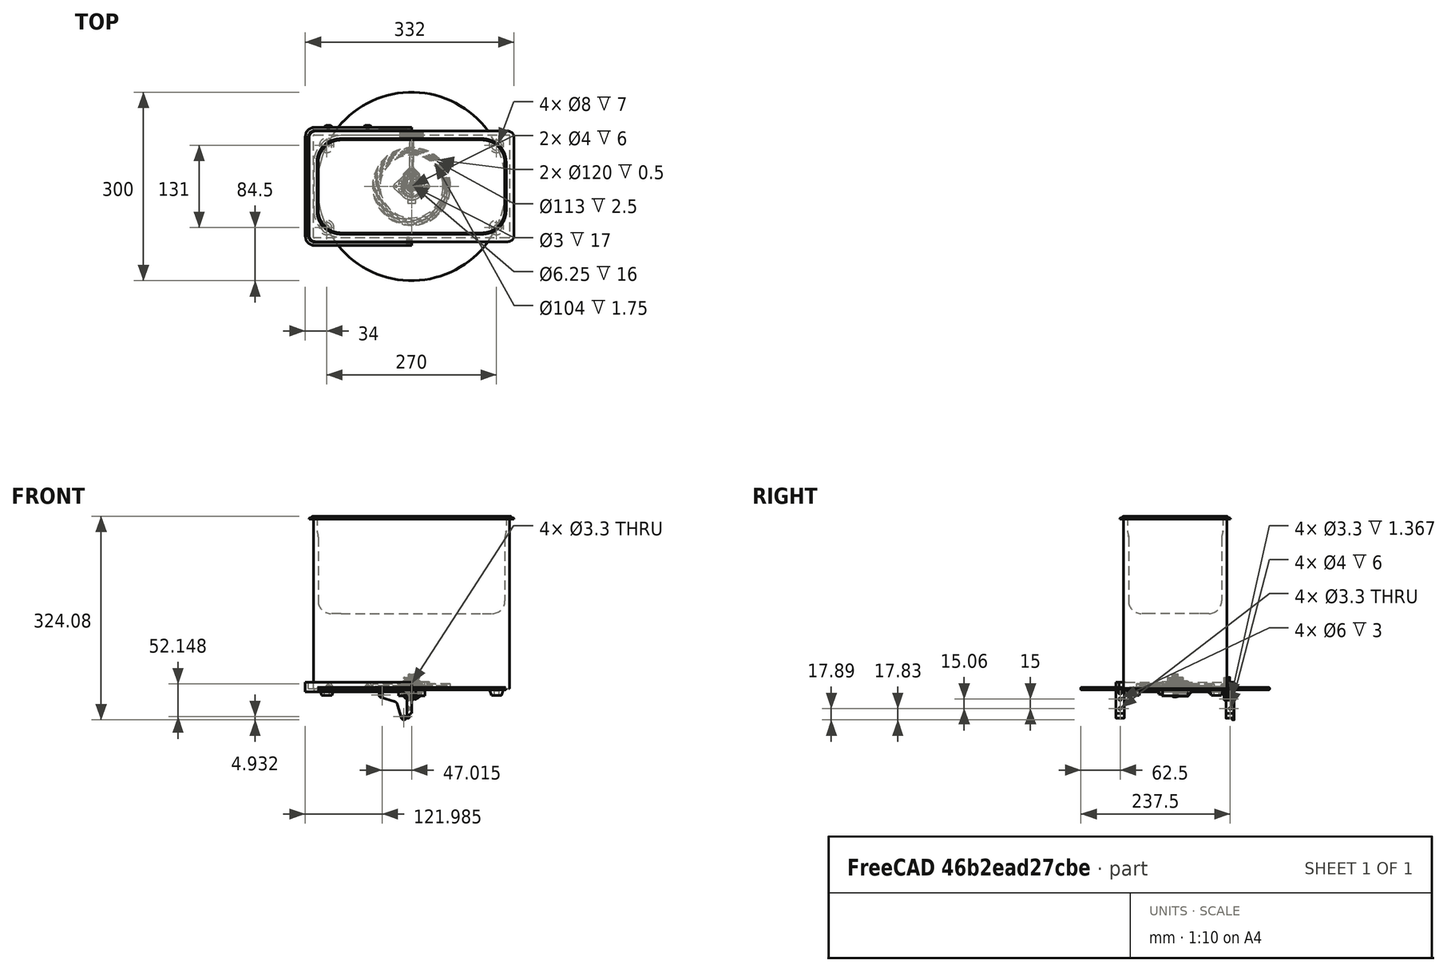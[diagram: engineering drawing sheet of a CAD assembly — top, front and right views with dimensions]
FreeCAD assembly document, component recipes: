
FREECAD ASSEMBLY — COMPONENT RECIPES ("assembly-ultrasonic-cleaner-exploded")

This assembly document has 14 components, labeled P0..P13 below (a component is one placed body or linked part). 14 of them carry a construction recipe — the FreeCAD feature program that regenerates the part from scratch, quoted from this document or its linked companion documents; the rest are supplied as boundary geometry only. No exploded tour is included for this assembly.
NOTE — this tour is split across 2 documents so each fits a 32k-token context. This is document 1: the component sections continue in the remaining 1 document, each repeating the header above.
COMPONENT P0 — recipe-attached ("Body", modeled in this document).
Construction recipe (the document's own serialized feature program — sketch geometry with constraints, then the solid features built on it; lengths are millimeters unless a unit is written):

FEATURE [Sketcher::SketchObject] CopySketch004
  ArcFitTolerance = 0
  ExternalBSplineMaxDegree = 0
  ExternalBSplineTolerance = 0
  FullyConstrained = false
  InternalTolerance = 1e-06
  InvalidShape = false
  MakeInternals = false
  Placement = pos=(0,0,250.5) rot=(0,0,1;0rad)
  TreeRank = 0
  ValidateShape = false
  sketch-geometry (8):
    g0: ArcOfCircle CenterX=112.315 CenterY=-37.8146 CenterZ=0 NormalX=0 NormalY=0 NormalZ=1 AngleXU=0 Radius=38.1854 StartAngle=4.71239 EndAngle=6.28319
    g1: ArcOfCircle CenterX=112.315 CenterY=37.8146 CenterZ=0 NormalX=0 NormalY=0 NormalZ=1 AngleXU=0 Radius=38.1854 StartAngle=2e-16 EndAngle=1.5708
    g2: ArcOfCircle CenterX=-112.315 CenterY=37.8146 CenterZ=0 NormalX=0 NormalY=0 NormalZ=1 AngleXU=0 Radius=38.1854 StartAngle=1.5708 EndAngle=3.14159
    g3: ArcOfCircle CenterX=-112.315 CenterY=-37.8146 CenterZ=0 NormalX=0 NormalY=0 NormalZ=1 AngleXU=0 Radius=38.1854 StartAngle=3.14159 EndAngle=4.71239
    g4: LineSegment StartX=150.5 StartY=-37.8146 StartZ=0 EndX=150.5 EndY=37.8146 EndZ=0
    g5: LineSegment StartX=112.315 StartY=-76 StartZ=0 EndX=-112.315 EndY=-76 EndZ=0
    g6: LineSegment StartX=-150.5 StartY=-37.8146 StartZ=0 EndX=-150.5 EndY=37.8146 EndZ=0
    g7: LineSegment StartX=112.315 StartY=76 StartZ=0 EndX=-112.315 EndY=76 EndZ=0
  constraints (14):
    c: Symmetric(g4,g6,g-2)
    c: Symmetric(g6,g4,g-2)
    c: Symmetric(g4,g4,g-1)
    c: Symmetric(g5,g7,g-1)
    c: Symmetric(g5,g7,g-1)
    c: Symmetric(g5,g5,g-2)
    c: Tangent(g0,g4) = -1.5708
    c: Tangent(g4,g1) = -1.5708
    c: Tangent(g1,g7) = -1.5708
    c: Tangent(g2,g7) = -1.5708
    c: Tangent(g6,g2) = 1.5708
    c: Tangent(g3,g6) = 1.5708
    c: Tangent(g3,g5) = 1.5708
    c: Tangent(g0,g5) = 1.5708
FEATURE [Sketcher::SketchObject] Sketch
  ArcFitTolerance = 0
  AttachmentSupport = -> [XY_Plane]
  ExternalBSplineMaxDegree = 0
  ExternalBSplineTolerance = 0
  FullyConstrained = false
  InternalTolerance = 1e-06
  InvalidShape = false
  MakeInternals = false
  MapMode = 5
  Support = -> [XY_Plane]
  TreeRank = 0
  ValidateShape = false
  sketch-geometry (4):
    g0: LineSegment StartX=-156 StartY=82 StartZ=0 EndX=156 EndY=82 EndZ=0
    g1: LineSegment StartX=156 StartY=82 StartZ=0 EndX=156 EndY=-82 EndZ=0
    g2: LineSegment StartX=156 StartY=-82 StartZ=0 EndX=-156 EndY=-82 EndZ=0
    g3: LineSegment StartX=-156 StartY=-82 StartZ=0 EndX=-156 EndY=82 EndZ=0
  constraints (10):
    c: Coincident(g0,g1)
    c: Coincident(g1,g2)
    c: Coincident(g2,g3)
    c: Coincident(g3,g0)
    c: Horizontal(g2)
    c: Vertical(g1)
    c: Symmetric(g0,g2,g-1)
    c: Symmetric(g0,g0,g-2)
    c: DistanceX(g0,g0) = 312
    c: DistanceY(g3,g3) = 164
FEATURE [PartDesign::Pad] Pad
  AddSubType = 0
  AllowMultiFace = false
  AutoTaperInnerAngle = true
  CheckUpToFaceLimits = true
  ClaimChildren = false
  Direction = (1,1,1)
  Fit = 0
  FitJoin = 0
  InnerFit = 0
  InnerFitJoin = 0
  InvalidShape = false
  Length = 270
  Length2 = 100
  NewSolid = false
  Profile = -> Sketch
  Suppress = false
  TaperInnerAngle = 0
  TaperInnerAngleRev = 0
  TreeRank = 0
  Type = 0
  ValidateShape = true
  _ProfileBasedVersion = 0
FEATURE [Sketcher::SketchObject] Sketch001
  ArcFitTolerance = 0
  AttachmentSupport = -> [Pad]
  ExternalBSplineMaxDegree = 0
  ExternalBSplineTolerance = 0
  FullyConstrained = false
  InternalTolerance = 1e-06
  InvalidShape = false
  MakeInternals = false
  MapMode = 5
  Placement = pos=(0,0,270) rot=(0,0,1;0rad)
  Support = -> [Pad]
  TreeRank = 0
  ValidateShape = false
  sketch-geometry (4):
    g0: LineSegment StartX=-163 StartY=88 StartZ=0 EndX=163 EndY=88 EndZ=0
    g1: LineSegment StartX=163 StartY=88 StartZ=0 EndX=163 EndY=-88 EndZ=0
    g2: LineSegment StartX=163 StartY=-88 StartZ=0 EndX=-163 EndY=-88 EndZ=0
    g3: LineSegment StartX=-163 StartY=-88 StartZ=0 EndX=-163 EndY=88 EndZ=0
  constraints (10):
    c: Coincident(g0,g1)
    c: Coincident(g1,g2)
    c: Coincident(g2,g3)
    c: Coincident(g3,g0)
    c: Horizontal(g2)
    c: Vertical(g1)
    c: DistanceX(g0,g0) = 326
    c: DistanceY(g3,g3) = 176
    c: Symmetric(g0,g2,g-1)
    c: Symmetric(g0,g0,g-2)
FEATURE [PartDesign::Pad] Pad001
  AddSubType = 0
  AllowMultiFace = false
  AutoTaperInnerAngle = true
  BaseFeature = -> Pad
  CheckUpToFaceLimits = true
  ClaimChildren = false
  Direction = (1,1,1)
  Fit = 0
  FitJoin = 0
  InnerFit = 0
  InnerFitJoin = 0
  InvalidShape = false
  Length = 1.5
  Length2 = 100
  NewSolid = false
  Profile = -> Sketch001
  Suppress = false
  TaperInnerAngle = 0
  TaperInnerAngleRev = 0
  TreeRank = 0
  Type = 0
  ValidateShape = true
  _ProfileBasedVersion = 0
FEATURE [PartDesign::Fillet] Fillet
  AddSubType = 0
  Base = -> Pad001 [Edge22,Edge18,Edge17,Edge20]
  BaseFeature = -> Pad001
  InvalidShape = false
  NewSolid = false
  Radius = 10
  SupportTransform = false
  Suppress = false
  TreeRank = 0
  UseAllEdges = false
  ValidateShape = true
FEATURE [Sketcher::SketchObject] Sketch002
  ArcFitTolerance = 0
  AttachmentSupport = -> [Fillet]
  ExternalBSplineMaxDegree = 0
  ExternalBSplineTolerance = 0
  ExternalGeometry = -> [Fillet]
  FullyConstrained = false
  InternalTolerance = 1e-06
  InvalidShape = false
  MakeInternals = false
  MapMode = 5
  Placement = pos=(0,0,271.5) rot=(0,0,1;0rad)
  Support = -> [Fillet]
  TreeRank = 0
  ValidateShape = false
  sketch-geometry (8):
    g0: LineSegment StartX=-158 StartY=78 StartZ=0 EndX=-158 EndY=-78 EndZ=0
    g1: LineSegment StartX=-153 StartY=-83 StartZ=0 EndX=153 EndY=-83 EndZ=0
    g2: LineSegment StartX=158 StartY=-78 StartZ=0 EndX=158 EndY=78 EndZ=0
    g3: LineSegment StartX=153 StartY=83 StartZ=0 EndX=-153 EndY=83 EndZ=0
    g4: ArcOfCircle CenterX=-153 CenterY=78 CenterZ=0 NormalX=0 NormalY=0 NormalZ=1 AngleXU=0 Radius=5 StartAngle=1.5708 EndAngle=3.14159
    g5: ArcOfCircle CenterX=-153 CenterY=-78 CenterZ=0 NormalX=0 NormalY=0 NormalZ=1 AngleXU=0 Radius=5 StartAngle=3.14159 EndAngle=4.71239
    g6: ArcOfCircle CenterX=153 CenterY=-78 CenterZ=0 NormalX=0 NormalY=0 NormalZ=1 AngleXU=0 Radius=5 StartAngle=4.71239 EndAngle=6.28319
    g7: ArcOfCircle CenterX=153 CenterY=78 CenterZ=0 NormalX=0 NormalY=0 NormalZ=1 AngleXU=0 Radius=5 StartAngle=-9e-16 EndAngle=1.5708
  constraints (17):
    c: Vertical(g0)
    c: Horizontal(g1)
    c: Symmetric(g1,g3,g-1)
    c: Symmetric(g3,g1,g-1)
    c: Symmetric(g0,g2,g-2)
    c: Symmetric(g2,g0,g-2)
    c: Tangent(g7,g3) = -1.5708
    c: Tangent(g7,g2) = -1.5708
    c: Tangent(g6,g2) = -1.5708
    c: Tangent(g1,g6) = -1.5708
    c: Tangent(g1,g5) = -1.5708
    c: Tangent(g5,g0) = -1.5708
    c: Tangent(g4,g0) = -1.5708
    c: Tangent(g4,g3) = -1.5708
    c: DistanceY(g3,g-10) = 5
    c: DistanceX(g-4,g0) = 5
    c: Horizontal(g-4,g0)
FEATURE [PartDesign::Pad] Pad002
  AddSubType = 0
  AllowMultiFace = false
  AutoTaperInnerAngle = true
  BaseFeature = -> Fillet
  CheckUpToFaceLimits = true
  ClaimChildren = false
  Direction = (1,1,1)
  Fit = 0
  FitJoin = 0
  InnerFit = 0
  InnerFitJoin = 0
  InvalidShape = false
  Length = 3
  Length2 = 100
  NewSolid = false
  Profile = -> Sketch002
  Suppress = false
  TaperInnerAngle = 0
  TaperInnerAngleRev = 0
  TreeRank = 0
  Type = 0
  ValidateShape = true
  _ProfileBasedVersion = 0
FEATURE [PartDesign::Draft] Draft
  AddSubType = 0
  Angle = 45
  Base = -> Pad002 [Face21,Face22,Face23,Face16,Face17,Face18,Face19,Face20]
  BaseFeature = -> Pad002
  InvalidShape = false
  NeutralPlane = -> Pad002 [Face24]
  NewSolid = false
  SupportTransform = false
  Suppress = false
  TreeRank = 0
  ValidateShape = true
FEATURE [PartDesign::Fillet] Fillet001
  AddSubType = 0
  Base = -> Draft [Edge59,Edge60,Edge44,Edge43,Edge42,Edge57,Edge55,Edge41,Edge53,Edge40,Edge51,Edge49,Edge38,Edge39,Edge47,Edge37]
  BaseFeature = -> Draft
  InvalidShape = false
  NewSolid = false
  Radius = 4
  SupportTransform = false
  Suppress = false
  TreeRank = 0
  UseAllEdges = false
  ValidateShape = true
FEATURE [Sketcher::SketchObject] Sketch003
  ArcFitTolerance = 0
  AttachmentSupport = -> [Fillet001]
  ExternalBSplineMaxDegree = 0
  ExternalBSplineTolerance = 0
  ExternalGeometry = -> [Fillet001]
  FullyConstrained = false
  InternalTolerance = 1e-06
  InvalidShape = false
  MakeInternals = false
  MapMode = 5
  Placement = pos=(0,0,274.5) rot=(0,0,1;0rad)
  Support = -> [Fillet001]
  TreeRank = 0
  ValidateShape = false
  sketch-geometry (9):
    g0: ArcOfCircle CenterX=-112.315 CenterY=37.8146 CenterZ=0 NormalX=0 NormalY=0 NormalZ=1 AngleXU=0 Radius=38.1854 StartAngle=1.5708 EndAngle=3.14159
    g1: ArcOfCircle CenterX=-112.315 CenterY=-37.8146 CenterZ=0 NormalX=0 NormalY=0 NormalZ=1 AngleXU=0 Radius=38.1854 StartAngle=3.14159 EndAngle=4.71239
    g2: ArcOfCircle CenterX=112.315 CenterY=-37.8146 CenterZ=0 NormalX=0 NormalY=0 NormalZ=1 AngleXU=0 Radius=38.1854 StartAngle=4.71239 EndAngle=6.28319
    g3: ArcOfCircle CenterX=112.315 CenterY=37.8146 CenterZ=0 NormalX=0 NormalY=0 NormalZ=1 AngleXU=0 Radius=38.1854 StartAngle=0 EndAngle=1.5708
    g4: LineSegment StartX=-150.5 StartY=37.8146 StartZ=0 EndX=-150.5 EndY=-37.8146 EndZ=0
    g5: LineSegment StartX=-112.315 StartY=76 StartZ=0 EndX=112.315 EndY=76 EndZ=0
    g6: LineSegment StartX=-112.315 StartY=-76 StartZ=0 EndX=112.315 EndY=-76 EndZ=0
    g7: LineSegment StartX=150.5 StartY=-37.8146 StartZ=0 EndX=150.5 EndY=37.8146 EndZ=0
    g8: LineSegment [constr] StartX=160.115 StartY=85.0272 StartZ=0 EndX=139.482 EndY=64.6483 EndZ=0
  constraints (21):
    c: Symmetric(g7,g4,g-2)
    c: Symmetric(g4,g7,g-2)
    c: Symmetric(g4,g4,g-1)
    c: Symmetric(g6,g6,g-2)
    c: Symmetric(g6,g5,g-1)
    c: Symmetric(g5,g6,g-1)
    c: Tangent(g0,g4) = -1.5708
    c: Tangent(g0,g5) = 1.5708
    c: Tangent(g4,g1) = -1.5708
    c: Tangent(g1,g6) = -1.5708
    c: Coincident(g2,g7)
    c: Tangent(g3,g5) = 1.5708
    c: Tangent(g3,g7) = -1.5708
    c: DistanceY(g3,g-5) = 12
    c: DistanceX(g3,g-6) = 12.5
    c: PointOnObject(g8,g-7)
    c: PointOnObject(g8,g3)
    c: Perpendicular(g-7,g8)
    c: Perpendicular(g3,g8)
    c: Distance(g8) = 29
    c: Tangent(g2,g6) = -1.5708
FEATURE [PartDesign::Pocket] Pocket
  AddSubType = 1
  AllowMultiFace = false
  AutoTaperInnerAngle = true
  BaseFeature = -> Fillet001
  CheckUpToFaceLimits = true
  ClaimChildren = false
  Direction = (1,1,1)
  Fit = 0
  FitJoin = 0
  InnerFit = 0
  InnerFitJoin = 0
  InvalidShape = false
  Length = 24
  Length2 = 100
  NewSolid = false
  Profile = -> Sketch003
  Suppress = false
  TaperInnerAngle = 0
  TaperInnerAngleRev = 0
  TreeRank = 0
  Type = 0
  ValidateShape = true
  _ProfileBasedVersion = 0
  _Version = 0
FEATURE [Sketcher::SketchObject] Sketch004
  ArcFitTolerance = 0
  AttachmentSupport = -> [Pocket]
  ExternalBSplineMaxDegree = 0
  ExternalBSplineTolerance = 0
  ExternalGeometry = -> [Pocket]
  FullyConstrained = false
  InternalTolerance = 1e-06
  InvalidShape = false
  MakeInternals = false
  MapMode = 5
  Placement = pos=(0,0,250.5) rot=(0,0,1;0rad)
  Support = -> [Pocket]
  TreeRank = 0
  ValidateShape = false
  sketch-geometry (8):
    g0: ArcOfCircle CenterX=112.315 CenterY=-37.8146 CenterZ=0 NormalX=0 NormalY=0 NormalZ=1 AngleXU=0 Radius=38.1854 StartAngle=4.71239 EndAngle=6.28319
    g1: ArcOfCircle CenterX=112.315 CenterY=37.8146 CenterZ=0 NormalX=0 NormalY=0 NormalZ=1 AngleXU=0 Radius=38.1854 StartAngle=2e-16 EndAngle=1.5708
    g2: ArcOfCircle CenterX=-112.315 CenterY=37.8146 CenterZ=0 NormalX=0 NormalY=0 NormalZ=1 AngleXU=0 Radius=38.1854 StartAngle=1.5708 EndAngle=3.14159
    g3: ArcOfCircle CenterX=-112.315 CenterY=-37.8146 CenterZ=0 NormalX=0 NormalY=0 NormalZ=1 AngleXU=0 Radius=38.1854 StartAngle=3.14159 EndAngle=4.71239
    g4: LineSegment StartX=150.5 StartY=-37.8146 StartZ=0 EndX=150.5 EndY=37.8146 EndZ=0
    g5: LineSegment StartX=112.315 StartY=-76 StartZ=0 EndX=-112.315 EndY=-76 EndZ=0
    g6: LineSegment StartX=-150.5 StartY=-37.8146 StartZ=0 EndX=-150.5 EndY=37.8146 EndZ=0
    g7: LineSegment StartX=112.315 StartY=76 StartZ=0 EndX=-112.315 EndY=76 EndZ=0
  constraints (17):
    c: Symmetric(g4,g6,g-2)
    c: Symmetric(g6,g4,g-2)
    c: Symmetric(g4,g4,g-1)
    c: Symmetric(g5,g7,g-1)
    c: Symmetric(g5,g7,g-1)
    c: Symmetric(g5,g5,g-2)
    c: Tangent(g0,g4) = -1.5708
    c: Tangent(g4,g1) = -1.5708
    c: Tangent(g1,g7) = -1.5708
    c: Tangent(g2,g7) = -1.5708
    c: Tangent(g6,g2) = 1.5708
    c: Tangent(g3,g6) = 1.5708
    c: Tangent(g3,g5) = 1.5708
    c: Tangent(g0,g5) = 1.5708
    c: DistanceY(g-8,g0) = 0
    c: DistanceX(g0,g-7) = 0
    c: Vertical(g0,g-8)
FEATURE [PartDesign::SubtractiveLoft] SubtractiveLoft
  AddSubType = 1
  AllowMultiFace = false
  BaseFeature = -> Pocket
  ClaimChildren = false
  Closed = false
  Fit = 0
  FitJoin = 0
  InnerFit = 0
  InnerFitJoin = 0
  InvalidShape = false
  MaxDegree = 5
  NewSolid = false
  Profile = -> CopySketch004
  Ruled = false
  Sections = -> [Sketch005]
  SplitProfile = false
  Suppress = false
  TreeRank = 0
  ValidateShape = true
  _ProfileBasedVersion = 0
FEATURE [PartDesign::Pocket] Pocket001
  AddSubType = 1
  AllowMultiFace = false
  AutoTaperInnerAngle = true
  BaseFeature = -> SubtractiveLoft
  CheckUpToFaceLimits = true
  ClaimChildren = false
  Direction = (1,1,1)
  Fit = 0
  FitJoin = 0
  InnerFit = 0
  InnerFitJoin = 0
  InvalidShape = false
  Length = 0
  Length2 = 100
  NewSolid = false
  Profile = -> CopySketch005
  Suppress = false
  TaperInnerAngle = 0
  TaperInnerAngleRev = 0
  TreeRank = 0
  Type = 3
  UpToFace = -> Plane001 [Face1]
  ValidateShape = true
  _ProfileBasedVersion = 0
  _Version = 0
FEATURE [PartDesign::Fillet] Fillet002
  AddSubType = 0
  Base = -> Pocket001 [Face50,Face51,Face49,Face56,Face55,Face54,Face53,Face52]
  BaseFeature = -> Pocket001
  InvalidShape = false
  NewSolid = false
  Radius = 10
  SupportTransform = false
  Suppress = false
  TreeRank = 0
  UseAllEdges = false
  ValidateShape = true
FEATURE [PartDesign::Fillet] Fillet003
  AddSubType = 0
  Base = -> Fillet002 [Face58]
  BaseFeature = -> Fillet002
  InvalidShape = false
  NewSolid = false
  Radius = 20
  SupportTransform = false
  Suppress = false
  TreeRank = 0
  UseAllEdges = false
  ValidateShape = true
FEATURE [Sketcher::SketchObject] Sketch006
  ArcFitTolerance = 0
  AttachmentSupport = -> [Fillet003]
  ExternalBSplineMaxDegree = 0
  ExternalBSplineTolerance = 0
  FullyConstrained = false
  InternalTolerance = 1e-06
  InvalidShape = false
  MakeInternals = false
  MapMode = 5
  Placement = pos=(0,0,0) rot=(1,0,0;3.14159rad)
  Support = -> [Fillet003]
  TreeRank = 0
  ValidateShape = false
  sketch-geometry (4):
    g0: Circle [constr] CenterX=-135 CenterY=65.5 CenterZ=0 NormalX=0 NormalY=0 NormalZ=1 AngleXU=0 Radius=11.5
    g1: Circle [constr] CenterX=135 CenterY=65.5 CenterZ=0 NormalX=0 NormalY=0 NormalZ=1 AngleXU=0 Radius=11.5
    g2: Circle CenterX=135 CenterY=-65.5 CenterZ=0 NormalX=0 NormalY=0 NormalZ=1 AngleXU=0 Radius=11.5
    g3: Circle [constr] CenterX=-135 CenterY=-65.5 CenterZ=0 NormalX=0 NormalY=0 NormalZ=1 AngleXU=0 Radius=11.5
  constraints (9):
    c: Symmetric(g0,g1,g-2)
    c: Symmetric(g3,g2,g-2)
    c: Symmetric(g3,g0,g-1)
    c: Equal(g0,g1)
    c: Equal(g1,g2)
    c: Equal(g2,g3)
    c: Diameter(g1) = 23
    c: DistanceY(g2,g1) = 131
    c: DistanceX(g3,g2) = 270
FEATURE [PartDesign::AdditiveLoft] AdditiveLoft
  AddSubType = 0
  AllowMultiFace = false
  BaseFeature = -> Fillet003
  ClaimChildren = false
  Closed = false
  Fit = 0
  FitJoin = 0
  InnerFit = 0
  InnerFitJoin = 0
  InvalidShape = false
  MaxDegree = 5
  NewSolid = false
  Profile = -> Sketch006
  Ruled = false
  Sections = -> [Sketch007]
  SplitProfile = false
  Suppress = false
  TreeRank = 0
  ValidateShape = true
  _ProfileBasedVersion = 0
FEATURE [Sketcher::SketchObject] Sketch008
  ArcFitTolerance = 0
  AttachmentSupport = -> [AdditiveLoft]
  ExternalBSplineMaxDegree = 0
  ExternalBSplineTolerance = 0
  ExternalGeometry = -> [AdditiveLoft]
  FullyConstrained = false
  InternalTolerance = 1e-06
  InvalidShape = false
  MakeInternals = false
  MapMode = 5
  Placement = pos=(-8e-16,-1.4e-15,-11) rot=(1,0,0;3.14159rad)
  Support = -> [AdditiveLoft]
  TreeRank = 0
  ValidateShape = false
  sketch-geometry (1):
    g0: Circle CenterX=135 CenterY=-65.5 CenterZ=0 NormalX=0 NormalY=0 NormalZ=1 AngleXU=0 Radius=4
  constraints (2):
    c: Coincident(g0,g-3)
    c: Diameter(g0) = 8
FEATURE [PartDesign::Pocket] Pocket002
  AddSubType = 1
  AllowMultiFace = false
  AutoTaperInnerAngle = true
  BaseFeature = -> AdditiveLoft
  CheckUpToFaceLimits = true
  ClaimChildren = false
  Direction = (1,1,1)
  Fit = 0
  FitJoin = 0
  InnerFit = 0
  InnerFitJoin = 0
  InvalidShape = false
  Length = 7
  Length2 = 100
  NewSolid = false
  Profile = -> Sketch008
  Suppress = false
  TaperInnerAngle = 0
  TaperInnerAngleRev = 0
  TreeRank = 0
  Type = 0
  ValidateShape = true
  _ProfileBasedVersion = 0
  _Version = 0
FEATURE [PartDesign::Mirrored] Mirrored001
  AddSubType = 0
  CopyShape = true
  InvalidShape = false
  MirrorPlane = -> Sketch006 [H_Axis]
  NewSolid = false
  ParallelTransform = true
  SubTransform = true
  Suppress = false
  TreeRank = 0
  ValidateShape = true
  _Version = 0
FEATURE [PartDesign::Mirrored] Mirrored
  AddSubType = 0
  CopyShape = true
  InvalidShape = false
  MirrorPlane = -> Sketch006 [V_Axis]
  NewSolid = false
  ParallelTransform = true
  SubTransform = true
  Suppress = false
  TreeRank = 0
  ValidateShape = true
  _Version = 0
FEATURE [PartDesign::MultiTransform] MultiTransform
  AddSubType = 0
  BaseFeature = -> Pocket002
  CopyShape = true
  InvalidShape = false
  NewSolid = false
  OriginalSubs = -> [AdditiveLoft,Pocket002]
  Originals = -> [AdditiveLoft,Pocket002]
  ParallelTransform = true
  SubTransform = true
  Suppress = false
  Transformations = -> [Mirrored,Mirrored001]
  TreeRank = 0
  ValidateShape = true
  _Version = 0
FEATURE [PartDesign::Fillet] Fillet004
  AddSubType = 0
  Base = -> MultiTransform [Edge190,Edge189,Edge191,Edge193,Edge195,Edge196,Edge194,Edge192]
  BaseFeature = -> MultiTransform
  InvalidShape = false
  NewSolid = false
  Radius = 1
  SupportTransform = false
  Suppress = false
  TreeRank = 0
  UseAllEdges = false
  ValidateShape = true
FEATURE [PartDesign::Fillet] Fillet005
  AddSubType = 0
  Base = -> Fillet004 [Edge1,Edge3,Edge5,Edge7,Edge8,Edge6,Edge4,Edge2]
  BaseFeature = -> Fillet004
  InvalidShape = false
  NewSolid = false
  Radius = 3
  SupportTransform = false
  Suppress = false
  TreeRank = 0
  UseAllEdges = false
  ValidateShape = true
FEATURE [PartDesign::Body] Body
  AutoGroupSolids = false
  ClaimAllChildren = false
  ExportMode = 0
  Group = -> [Sketch,Pad,Sketch001,Pad001,Fillet,Sketch002,Pad002,Draft,Fillet001,Sketch003,Pocket,Sketch004,CopySketch004,SubtractiveLoft,Pocket001,Fillet002,Fillet003,Sketch006,AdditiveLoft,Sketch008,Pocket002,MultiTransform,Mirrored,Mirrored001,Fillet004,Fillet005]
  InvalidShape = false
  Origin = -> Origin
  SingleSolid = true
  Tip = -> Fillet005
  TreeRank = 0
  ValidateShape = false
  _ExportChildren = -> [Pad,Pad001,Fillet,Pad002,Draft,Fillet001,Pocket,Sketch004,SubtractiveLoft,Pocket001,Fillet002,Fillet003,AdditiveLoft,Pocket002,MultiTransform,Fillet004,Fillet005]
  _GroupVersion = 1
COMPONENT P1 — recipe-attached ("Body001", modeled in this document).
Construction recipe (the document's own serialized feature program — sketch geometry with constraints, then the solid features built on it; lengths are millimeters unless a unit is written):

FEATURE [Sketcher::SketchObject] Sketch018
  ArcFitTolerance = 0
  AttachmentSupport = -> [XY_Plane001]
  ExternalBSplineMaxDegree = 0
  ExternalBSplineTolerance = 0
  FullyConstrained = false
  InternalTolerance = 1e-06
  InvalidShape = false
  MakeInternals = false
  MapMode = 5
  Support = -> [XY_Plane001]
  TreeRank = 0
  ValidateShape = false
  sketch-geometry (16):
    g0: LineSegment StartX=-154 StartY=89 StartZ=0 EndX=154 EndY=89 EndZ=0
    g1: LineSegment StartX=164 StartY=79 StartZ=0 EndX=164 EndY=-79 EndZ=0
    g2: LineSegment StartX=154 StartY=-89 StartZ=0 EndX=-154 EndY=-89 EndZ=0
    g3: LineSegment StartX=-164 StartY=-79 StartZ=0 EndX=-164 EndY=79 EndZ=0
    g4: ArcOfCircle CenterX=-154 CenterY=79 CenterZ=0 NormalX=0 NormalY=0 NormalZ=1 AngleXU=0 Radius=10 StartAngle=1.5708 EndAngle=3.14159
    g5: ArcOfCircle CenterX=154 CenterY=79 CenterZ=0 NormalX=0 NormalY=0 NormalZ=1 AngleXU=0 Radius=10 StartAngle=-9e-16 EndAngle=1.5708
    g6: ArcOfCircle CenterX=154 CenterY=-79 CenterZ=0 NormalX=0 NormalY=0 NormalZ=1 AngleXU=0 Radius=10 StartAngle=4.71239 EndAngle=6.28319
    g7: ArcOfCircle CenterX=-154 CenterY=-79 CenterZ=0 NormalX=0 NormalY=0 NormalZ=1 AngleXU=0 Radius=10 StartAngle=3.14159 EndAngle=4.71239
    g8: LineSegment StartX=-154 StartY=94 StartZ=0 EndX=154 EndY=94 EndZ=0
    g9: LineSegment StartX=169 StartY=79 StartZ=0 EndX=169 EndY=-79 EndZ=0
    g10: LineSegment StartX=154 StartY=-94 StartZ=0 EndX=-154 EndY=-94 EndZ=0
    g11: LineSegment StartX=-169 StartY=-79 StartZ=0 EndX=-169 EndY=79 EndZ=0
    g12: ArcOfCircle CenterX=-154 CenterY=79 CenterZ=0 NormalX=0 NormalY=0 NormalZ=1 AngleXU=0 Radius=15 StartAngle=1.5708 EndAngle=3.14159
    g13: ArcOfCircle CenterX=154 CenterY=79 CenterZ=0 NormalX=0 NormalY=0 NormalZ=1 AngleXU=0 Radius=15 StartAngle=1e-16 EndAngle=1.5708
    g14: ArcOfCircle CenterX=154 CenterY=-79 CenterZ=0 NormalX=0 NormalY=0 NormalZ=1 AngleXU=0 Radius=15 StartAngle=4.71239 EndAngle=6.28319
    g15: ArcOfCircle CenterX=-154 CenterY=-79 CenterZ=0 NormalX=0 NormalY=0 NormalZ=1 AngleXU=0 Radius=15 StartAngle=3.14159 EndAngle=4.71239
  constraints (35):
    c: Tangent(g3,g4) = 1.5708
    c: Tangent(g0,g4) = 1.5708
    c: Tangent(g0,g5) = 1.5708
    c: Tangent(g1,g5) = 1.5708
    c: Tangent(g1,g6) = 1.5708
    c: Tangent(g2,g6) = 1.5708
    c: Tangent(g2,g7) = 1.5708
    c: Tangent(g3,g7) = 1.5708
    c: Equal(g5,g6)
    c: Equal(g6,g7)
    c: Equal(g7,g4)
    c: Symmetric(g3,g1,g-2)
    c: Symmetric(g3,g1,g-2)
    c: Symmetric(g3,g3,g-1)
    c: DistanceX(g3,g1) = 328
    c: DistanceY(g2,g0) = 178
    c: Radius(g5) = 10
    c: Tangent(g11,g12) = 1.5708
    c: Tangent(g8,g12) = 1.5708
    c: Tangent(g8,g13) = 1.5708
    c: Tangent(g9,g13) = 1.5708
    c: Tangent(g9,g14) = 1.5708
    c: Tangent(g10,g14) = 1.5708
    c: Tangent(g10,g15) = 1.5708
    c: Tangent(g11,g15) = 1.5708
    c: Horizontal(g8)
    c: Horizontal(g10)
    c: Vertical(g9)
    c: Vertical(g11)
    c: DistanceX(g11,g3) = 5
    c: DistanceY(g0,g8) = 5
    c: Equal(g14,g13)
    c: Equal(g13,g12)
    c: Coincident(g15,g7)
    c: Coincident(g13,g5)
FEATURE [PartDesign::Pad] Pad007
  AddSubType = 0
  AutoTaperInnerAngle = true
  CheckUpToFaceLimits = true
  ClaimChildren = false
  Direction = (1,1,1)
  Fit = 0
  FitJoin = 0
  InnerFit = 0
  InnerFitJoin = 0
  InvalidShape = false
  Length = 10
  Length2 = 100
  NewSolid = false
  Profile = -> Sketch018
  Suppress = false
  TaperInnerAngle = 0
  TaperInnerAngleRev = 0
  TreeRank = 0
  Type = 0
  ValidateShape = true
  _ProfileBasedVersion = 0
FEATURE [PartDesign::Pad] Pad006
  AddSubType = 0
  AutoTaperInnerAngle = true
  BaseFeature = -> Pad007
  CheckUpToFaceLimits = true
  ClaimChildren = false
  Direction = (0,0,1)
  Fit = 0
  FitJoin = 0
  InnerFit = 0
  InnerFitJoin = 0
  InvalidShape = false
  Length = 5
  Length2 = 100
  NewSolid = false
  Profile = -> Sketch019
  Reversed = true
  Suppress = false
  TaperInnerAngle = 0
  TaperInnerAngleRev = 0
  TreeRank = 0
  Type = 0
  ValidateShape = true
  _ProfileBasedVersion = 0
FEATURE [Sketcher::SketchObject] Sketch017
  ArcFitTolerance = 0
  AttachmentSupport = -> [Pad006]
  ExternalBSplineMaxDegree = 0
  ExternalBSplineTolerance = 0
  ExternalGeometry = -> [Pad006]
  FullyConstrained = true
  InternalTolerance = 1e-06
  InvalidShape = false
  MakeInternals = false
  MapMode = 5
  Placement = pos=(0,94,0) rot=(0,0.707107,0.707107;3.14159rad)
  Support = -> [Pad006]
  TreeRank = 0
  ValidateShape = false
  sketch-geometry (6):
    g0: LineSegment StartX=-7.36667 StartY=-5 StartZ=0 EndX=7.36667 EndY=-5 EndZ=0
    g1: LineSegment StartX=-7.36667 StartY=-5 StartZ=0 EndX=-7.36667 EndY=-45 EndZ=0
    g2: LineSegment StartX=7.36667 StartY=-45 StartZ=0 EndX=7.36667 EndY=-5 EndZ=0
    g3: ArcOfCircle CenterX=5.36667 CenterY=-45 CenterZ=0 NormalX=0 NormalY=0 NormalZ=1 AngleXU=0 Radius=2 StartAngle=2.77438 EndAngle=6.28319
    g4: ArcOfCircle CenterX=-1e-16 CenterY=-42.9357 CenterZ=0 NormalX=0 NormalY=0 NormalZ=1 AngleXU=0 Radius=3.75 StartAngle=5.91598 EndAngle=9.79199
    g5: ArcOfCircle CenterX=-5.36667 CenterY=-45 CenterZ=0 NormalX=0 NormalY=0 NormalZ=1 AngleXU=0 Radius=2 StartAngle=3.14159 EndAngle=6.65039
  constraints (15):
    c: Symmetric(g0,g0,g-2)
    c: Coincident(g1,g0)
    c: Vertical(g1)
    c: Coincident(g2,g0)
    c: PointOnObject(g0,g-4)
    c: Symmetric(g2,g1,g-2)
    c: Tangent(g3,g2) = -1.5708
    c: Coincident(g5,g4)
    c: Tangent(g1,g5) = -1.5708
    c: Symmetric(g3,g4,g-2)
    c: Tangent(g4,g3) = 1.5708
    c: Diameter(g4) = 7.5
    c: Radius(g3) = 2
    c: DistanceX(g4,g3) = 7
    c: DistanceY(g1,g1) = 40
FEATURE [PartDesign::Pad] Pad005
  AddSubType = 0
  AutoTaperInnerAngle = true
  BaseFeature = -> Pad006
  CheckUpToFaceLimits = true
  ClaimChildren = false
  Direction = (0,1,-2e-16)
  Fit = 0
  FitJoin = 0
  InnerFit = 0
  InnerFitJoin = 0
  InvalidShape = false
  Length = 10
  Length2 = 100
  NewSolid = false
  Profile = -> Sketch017
  Reversed = true
  Suppress = false
  TaperInnerAngle = 0
  TaperInnerAngleRev = 0
  TreeRank = 0
  Type = 3
  UpToFace = -> Pad006 [Face27]
  ValidateShape = true
  _ProfileBasedVersion = 0
FEATURE [PartDesign::Mirrored] Mirrored003
  AddSubType = 0
  BaseFeature = -> Pad005
  CopyShape = true
  InvalidShape = false
  MirrorPlane = -> XZ_Plane001
  NewSolid = false
  OriginalSubs = -> [Pad005]
  Originals = -> [Pad005]
  ParallelTransform = true
  SubTransform = true
  Suppress = false
  TreeRank = 0
  ValidateShape = true
  _Version = 0
FEATURE [PartDesign::Fillet] Fillet006
  AddSubType = 0
  Base = -> Mirrored003 [Edge104,Edge36,Edge42,Edge100]
  BaseFeature = -> Mirrored003
  InvalidShape = false
  NewSolid = false
  Radius = 10
  SupportTransform = true
  Suppress = false
  TreeRank = 0
  UseAllEdges = false
  ValidateShape = true
FEATURE [Sketcher::SketchObject] Sketch016
  ArcFitTolerance = 0
  AttachmentSupport = -> [Fillet006]
  ExternalBSplineMaxDegree = 0
  ExternalBSplineTolerance = 0
  ExternalGeometry = -> [Fillet006]
  FullyConstrained = true
  InternalTolerance = 1e-06
  InvalidShape = false
  MakeInternals = false
  MapMode = 5
  Placement = pos=(0,94,-3.37e-14) rot=(0,0.707107,0.707107;3.14159rad)
  Support = -> [Fillet006]
  TreeRank = 0
  ValidateShape = false
  sketch-geometry (4):
    g0: LineSegment StartX=-5.36666 StartY=-47 StartZ=0 EndX=5.36667 EndY=-47 EndZ=0
    g1: ArcOfCircle CenterX=-5.36667 CenterY=-45 CenterZ=0 NormalX=0 NormalY=0 NormalZ=1 AngleXU=0 Radius=2 StartAngle=4.71239 EndAngle=6.65039
    g2: ArcOfCircle CenterX=5.36667 CenterY=-45 CenterZ=0 NormalX=0 NormalY=0 NormalZ=1 AngleXU=0 Radius=2 StartAngle=2.77438 EndAngle=4.71239
    g3: ArcOfCircle CenterX=7e-16 CenterY=-42.9357 CenterZ=0 NormalX=0 NormalY=0 NormalZ=1 AngleXU=0 Radius=3.75 StartAngle=5.91598 EndAngle=9.79199
  constraints (11):
    c: Tangent(g0,g-3)
    c: Coincident(g1,g0)
    c: Coincident(g1,g-3)
    c: Coincident(g1,g-4)
    c: Coincident(g2,g0)
    c: Coincident(g2,g-5)
    c: Coincident(g2,g-5)
    c: Tangent(g0,g-5)
    c: Coincident(g3,g2)
    c: Coincident(g3,g1)
    c: Coincident(g3,g-4)
FEATURE [PartDesign::Pad] Pad003
  AddSubType = 0
  AutoTaperInnerAngle = true
  BaseFeature = -> Fillet006
  CheckUpToFaceLimits = true
  ClaimChildren = false
  Direction = (0,1,-4e-16)
  Fit = 0
  FitJoin = 0
  InnerFit = 0
  InnerFitJoin = 0
  InvalidShape = false
  Length = 1.5
  Length2 = 100
  NewSolid = false
  Profile = -> Sketch016
  Reversed = true
  Suppress = false
  TaperInnerAngle = 0
  TaperInnerAngleRev = 0
  TreeRank = 0
  Type = 0
  ValidateShape = true
  _ProfileBasedVersion = 0
FEATURE [PartDesign::Mirrored] Mirrored002
  AddSubType = 0
  BaseFeature = -> Pad003
  CopyShape = true
  InvalidShape = false
  MirrorPlane = -> XZ_Plane001
  NewSolid = false
  OriginalSubs = -> [Pad003]
  Originals = -> [Pad003]
  ParallelTransform = true
  SubTransform = true
  Suppress = false
  TreeRank = 0
  ValidateShape = true
  _Version = 0
FEATURE [PartDesign::Chamfer] Chamfer002
  AddSubType = 0
  Angle = 45
  Base = -> Mirrored002 [Edge114]
  BaseFeature = -> Mirrored002
  ChamferType = 0
  FlipDirection = false
  InvalidShape = false
  NewSolid = false
  Size = 0.1
  Size2 = 1
  SupportTransform = true
  Suppress = false
  TreeRank = 0
  UseAllEdges = false
  ValidateShape = true
FEATURE [Sketcher::SketchObject] Sketch015
  ArcFitTolerance = 0
  AttachmentSupport = -> [Chamfer002]
  ExternalBSplineMaxDegree = 0
  ExternalBSplineTolerance = 0
  FullyConstrained = false
  InternalTolerance = 1e-06
  InvalidShape = false
  MakeInternals = false
  MapMode = 5
  Placement = pos=(0,0,10) rot=(0,0,1;0rad)
  Support = -> [Chamfer002]
  TreeRank = 0
  ValidateShape = false
  sketch-geometry (4):
    g0: LineSegment StartX=0 StartY=119.45 StartZ=0 EndX=0 EndY=-119.45 EndZ=0
    g1: LineSegment StartX=0 StartY=119.45 StartZ=0 EndX=200.233 EndY=119.45 EndZ=0
    g2: LineSegment StartX=200.233 StartY=119.45 StartZ=0 EndX=200.233 EndY=-119.45 EndZ=0
    g3: LineSegment StartX=200.233 StartY=-119.45 StartZ=0 EndX=0 EndY=-119.45 EndZ=0
  constraints (9):
    c: PointOnObject(g0,g-2)
    c: Symmetric(g0,g0,g-1)
    c: Coincident(g0,g1)
    c: Horizontal(g1)
    c: Coincident(g1,g2)
    c: Vertical(g2)
    c: Coincident(g2,g3)
    c: Coincident(g3,g0)
    c: Horizontal(g3)
FEATURE [PartDesign::Pocket] Pocket010
  AddSubType = 1
  AutoTaperInnerAngle = true
  BaseFeature = -> Chamfer002
  CheckUpToFaceLimits = true
  ClaimChildren = false
  Direction = (0,0,-1)
  Fit = 0
  FitJoin = 0
  InnerFit = 0
  InnerFitJoin = 0
  InvalidShape = false
  Length = 5
  Length2 = 100
  NewSolid = false
  Profile = -> Sketch015
  Suppress = false
  TaperInnerAngle = 0
  TaperInnerAngleRev = 0
  TreeRank = 0
  Type = 1
  ValidateShape = true
  _ProfileBasedVersion = 0
  _Version = 0
FEATURE [Sketcher::SketchObject] Sketch014
  ArcFitTolerance = 0
  AttachmentSupport = -> [Pocket010]
  ExternalBSplineMaxDegree = 0
  ExternalBSplineTolerance = 0
  FullyConstrained = true
  InternalTolerance = 1e-06
  InvalidShape = false
  MakeInternals = false
  MapMode = 5
  Placement = pos=(0,0,0) rot=(0.57735,0.57735,0.57735;2.0944rad)
  Support = -> [Pocket010]
  TreeRank = 0
  ValidateShape = false
  sketch-geometry (1):
    g0: Circle CenterX=87.5 CenterY=-5 CenterZ=0 NormalX=0 NormalY=0 NormalZ=1 AngleXU=0 Radius=2
  constraints (3):
    c: Diameter(g0) = 4
    c: DistanceY(g0,g-1) = 5
    c: DistanceX(g-1,g0) = 87.5
FEATURE [PartDesign::Pad] Pad004
  AddSubType = 0
  AutoTaperInnerAngle = true
  BaseFeature = -> Pocket010
  CheckUpToFaceLimits = true
  ClaimChildren = false
  Direction = (1,0,0)
  Fit = 0
  FitJoin = 0
  InnerFit = 0
  InnerFitJoin = 0
  InvalidShape = false
  Length = 5
  Length2 = 100
  NewSolid = false
  Profile = -> Sketch014
  Suppress = false
  TaperInnerAngle = 0
  TaperInnerAngleRev = 0
  TreeRank = 0
  Type = 0
  ValidateShape = true
  _ProfileBasedVersion = 0
FEATURE [Sketcher::SketchObject] Sketch013
  ArcFitTolerance = 0
  AttachmentSupport = -> [Pad004]
  ExternalBSplineMaxDegree = 0
  ExternalBSplineTolerance = 0
  FullyConstrained = true
  InternalTolerance = 1e-06
  InvalidShape = false
  MakeInternals = false
  MapMode = 5
  Placement = pos=(0,0,0) rot=(0.57735,0.57735,0.57735;2.0944rad)
  Support = -> [Pad004]
  TreeRank = 0
  ValidateShape = false
  sketch-geometry (1):
    g0: Circle CenterX=-87.5 CenterY=-5 CenterZ=0 NormalX=0 NormalY=0 NormalZ=1 AngleXU=0 Radius=2.5
  constraints (3):
    c: Diameter(g0) = 5
    c: DistanceY(g0,g-1) = 5
    c: DistanceX(g0,g-1) = 87.5
FEATURE [PartDesign::Pocket] Pocket009
  AddSubType = 1
  AutoTaperInnerAngle = true
  BaseFeature = -> Pad004
  CheckUpToFaceLimits = true
  ClaimChildren = false
  Direction = (-1,0,0)
  Fit = 0
  FitJoin = 0
  InnerFit = 0
  InnerFitJoin = 0
  InvalidShape = false
  Length = 5.5
  Length2 = 100
  NewSolid = false
  Profile = -> Sketch013
  Suppress = false
  TaperInnerAngle = 0
  TaperInnerAngleRev = 0
  TreeRank = 0
  Type = 0
  ValidateShape = true
  _ProfileBasedVersion = 0
  _Version = 0
FEATURE [PartDesign::Chamfer] Chamfer003
  AddSubType = 0
  Angle = 45
  Base = -> Pocket009 [Edge84,Edge115]
  BaseFeature = -> Pocket009
  ChamferType = 0
  FlipDirection = false
  InvalidShape = false
  NewSolid = false
  Size = 1
  Size2 = 1
  SupportTransform = true
  Suppress = false
  TreeRank = 0
  UseAllEdges = false
  ValidateShape = true
FEATURE [Sketcher::SketchObject] Sketch012
  ArcFitTolerance = 0
  AttachmentSupport = -> [Chamfer003]
  ExternalBSplineMaxDegree = 0
  ExternalBSplineTolerance = 0
  FullyConstrained = true
  InternalTolerance = 1e-06
  InvalidShape = false
  MakeInternals = false
  MapMode = 5
  Placement = pos=(0,0,0) rot=(0.57735,0.57735,0.57735;2.0944rad)
  Support = -> [Chamfer003]
  TreeRank = 0
  ValidateShape = false
  sketch-geometry (4):
    g0: Circle CenterX=87.5 CenterY=-16.69 CenterZ=0 NormalX=0 NormalY=0 NormalZ=1 AngleXU=0 Radius=1.65
    g1: Circle CenterX=87.5 CenterY=-31.69 CenterZ=0 NormalX=0 NormalY=0 NormalZ=1 AngleXU=0 Radius=1.65
    g2: Circle CenterX=-87.5 CenterY=-16.69 CenterZ=0 NormalX=0 NormalY=0 NormalZ=1 AngleXU=0 Radius=1.65
    g3: Circle CenterX=-87.5 CenterY=-31.69 CenterZ=0 NormalX=0 NormalY=0 NormalZ=1 AngleXU=0 Radius=1.65
  constraints (10):
    c: Equal(g1,g0)
    c: Equal(g2,g3)
    c: Equal(g3,g0)
    c: Symmetric(g2,g0,g-2)
    c: Symmetric(g3,g1,g-2)
    c: Diameter(g0) = 3.3
    c: DistanceY(g0,g-1) = 16.69
    c: DistanceY(g1,g-1) = 31.69
    c: DistanceX(g-1,g0) = 87.5
    c: DistanceX(g-1,g1) = 87.5
FEATURE [PartDesign::Pocket] Pocket008
  AddSubType = 1
  AutoTaperInnerAngle = true
  BaseFeature = -> Chamfer003
  CheckUpToFaceLimits = true
  ClaimChildren = false
  Direction = (-1,0,0)
  Fit = 0
  FitJoin = 0
  InnerFit = 0
  InnerFitJoin = 0
  InvalidShape = false
  Length = 5
  Length2 = 100
  NewSolid = false
  Profile = -> Sketch012
  Suppress = false
  TaperInnerAngle = 0
  TaperInnerAngleRev = 0
  TreeRank = 0
  Type = 1
  ValidateShape = true
  _ProfileBasedVersion = 0
  _Version = 0
FEATURE [Sketcher::SketchObject] Sketch011
  ArcFitTolerance = 0
  AttachmentSupport = -> [Pocket008]
  ExternalBSplineMaxDegree = 0
  ExternalBSplineTolerance = 0
  FullyConstrained = true
  InternalTolerance = 1e-06
  InvalidShape = false
  MakeInternals = false
  MapMode = 5
  Placement = pos=(-7.36667,0,0) rot=(0.57735,-0.57735,-0.57735;2.0944rad)
  Support = -> [Pocket008]
  TreeRank = 0
  ValidateShape = false
  sketch-geometry (2):
    g0: Circle CenterX=-87.5 CenterY=-16.75 CenterZ=0 NormalX=0 NormalY=0 NormalZ=1 AngleXU=0 Radius=2
    g1: Circle CenterX=-87.5 CenterY=-31.75 CenterZ=0 NormalX=0 NormalY=0 NormalZ=1 AngleXU=0 Radius=2
  constraints (6):
    c: Equal(g1,g0)
    c: Diameter(g0) = 4
    c: DistanceY(g0,g-1) = 16.75
    c: DistanceX(g0,g-1) = 87.5
    c: Vertical(g1,g0)
    c: DistanceY(g1,g0) = 15
FEATURE [PartDesign::Pocket] Pocket003
  AddSubType = 1
  AutoTaperInnerAngle = true
  BaseFeature = -> Pocket008
  CheckUpToFaceLimits = true
  ClaimChildren = false
  Direction = (1,0,0)
  Fit = 0
  FitJoin = 0
  InnerFit = 0
  InnerFitJoin = 0
  InvalidShape = false
  Length = 6
  Length2 = 100
  NewSolid = false
  Profile = -> Sketch011
  Suppress = false
  TaperInnerAngle = 0
  TaperInnerAngleRev = 0
  TreeRank = 0
  Type = 0
  ValidateShape = true
  _ProfileBasedVersion = 0
  _Version = 0
FEATURE [PartDesign::Pocket] Pocket004
  AddSubType = 1
  AutoTaperInnerAngle = true
  BaseFeature = -> Pocket003
  CheckUpToFaceLimits = true
  ClaimChildren = false
  Direction = (1,0,0)
  Fit = 0
  FitJoin = 0
  InnerFit = 0
  InnerFitJoin = 0
  InvalidShape = false
  Length = 5
  Length2 = 100
  NewSolid = false
  Profile = -> Sketch011
  Reversed = true
  Suppress = false
  TaperInnerAngle = 0
  TaperInnerAngleRev = 0
  TreeRank = 0
  Type = 1
  ValidateShape = true
  _ProfileBasedVersion = 0
  _Version = 0
FEATURE [Sketcher::SketchObject] Sketch009
  ArcFitTolerance = 0
  AttachmentSupport = -> [Pocket004]
  ExternalBSplineMaxDegree = 0
  ExternalBSplineTolerance = 0
  FullyConstrained = true
  InternalTolerance = 1e-06
  InvalidShape = false
  MakeInternals = false
  MapMode = 5
  Placement = pos=(-7.36667,0,0) rot=(0.57735,-0.57735,-0.57735;2.0944rad)
  Support = -> [Pocket004]
  TreeRank = 0
  ValidateShape = false
  sketch-geometry (2):
    g0: Circle CenterX=87.5 CenterY=-16.69 CenterZ=0 NormalX=0 NormalY=0 NormalZ=1 AngleXU=0 Radius=3
    g1: Circle CenterX=87.5 CenterY=-31.69 CenterZ=0 NormalX=0 NormalY=0 NormalZ=1 AngleXU=0 Radius=3
  constraints (6):
    c: Equal(g0,g1)
    c: Diameter(g0) = 6
    c: DistanceX(g-1,g0) = 87.5
    c: DistanceY(g0,g-1) = 16.69
    c: DistanceY(g1,g-1) = 31.69
    c: Vertical(g1,g0)
FEATURE [PartDesign::Pocket] Pocket005
  AddSubType = 1
  AutoTaperInnerAngle = true
  BaseFeature = -> Pocket004
  CheckUpToFaceLimits = true
  ClaimChildren = false
  Direction = (1,0,0)
  Fit = 0
  FitJoin = 0
  InnerFit = 0
  InnerFitJoin = 0
  InvalidShape = false
  Length = 3
  Length2 = 100
  NewSolid = false
  Profile = -> Sketch009
  Suppress = false
  TaperInnerAngle = 0
  TaperInnerAngleRev = 0
  TreeRank = 0
  Type = 0
  ValidateShape = true
  _ProfileBasedVersion = 0
  _Version = 0
FEATURE [PartDesign::Pocket] Pocket006
  AddSubType = 1
  AutoTaperInnerAngle = true
  BaseFeature = -> Pocket005
  CheckUpToFaceLimits = true
  ClaimChildren = false
  Direction = (1,0,0)
  Fit = 0
  FitJoin = 0
  InnerFit = 0
  InnerFitJoin = 0
  InvalidShape = false
  Length = 5
  Length2 = 100
  NewSolid = false
  Profile = -> Sketch009
  Reversed = true
  Suppress = false
  TaperInnerAngle = 0
  TaperInnerAngleRev = 0
  TreeRank = 0
  Type = 1
  ValidateShape = true
  _ProfileBasedVersion = 0
  _Version = 0
FEATURE [PartDesign::Pocket] Pocket007
  AddSubType = 1
  AutoTaperInnerAngle = true
  BaseFeature = -> Pocket006
  CheckUpToFaceLimits = true
  ClaimChildren = false
  Direction = (0,1,0)
  Fit = 0
  FitJoin = 0
  InnerFit = 0
  InnerFitJoin = 0
  InvalidShape = false
  Length = 5
  Length2 = 100
  Midplane = true
  NewSolid = false
  Profile = -> Pocket006 [Face17]
  Suppress = false
  TaperInnerAngle = 0
  TaperInnerAngleRev = 0
  TreeRank = 0
  Type = 1
  ValidateShape = true
  _ProfileBasedVersion = 0
  _Version = 0
FEATURE [Sketcher::SketchObject] Sketch010
  ArcFitTolerance = 0
  AttachmentSupport = -> [Pocket007]
  ExternalBSplineMaxDegree = 0
  ExternalBSplineTolerance = 0
  ExternalGeometry = -> [Pocket007]
  FullyConstrained = true
  InternalTolerance = 1e-06
  InvalidShape = false
  MakeInternals = false
  MapMode = 5
  Placement = pos=(0,94,-3.37e-14) rot=(0,0.707107,0.707107;3.14159rad)
  Support = -> [Pocket007]
  TreeRank = 0
  ValidateShape = false
  sketch-geometry (9):
    g0: LineSegment StartX=7.36667 StartY=-15 StartZ=0 EndX=7.36667 EndY=-44.6482 EndZ=0
    g1: ArcOfCircle CenterX=17.3667 CenterY=-15 CenterZ=0 NormalX=0 NormalY=0 NormalZ=1 AngleXU=0 Radius=10 StartAngle=1.5708 EndAngle=3.14159
    g2: LineSegment StartX=17.3667 StartY=-5 StartZ=0 EndX=47.0149 EndY=-5 EndZ=0
    g3: ArcOfCircle CenterX=47.0149 CenterY=-10 CenterZ=0 NormalX=0 NormalY=0 NormalZ=1 AngleXU=0 Radius=5 StartAngle=5.49779 EndAngle=7.85398
    g4: ArcOfCircle CenterX=12.3667 CenterY=-44.6482 CenterZ=0 NormalX=0 NormalY=0 NormalZ=1 AngleXU=0 Radius=5 StartAngle=3.14159 EndAngle=5.49779
    g5: LineSegment StartX=50.5504 StartY=-13.5355 StartZ=0 EndX=15.9022 EndY=-48.1838 EndZ=0
    g6: LineSegment [constr] StartX=12.3667 StartY=-44.6482 StartZ=0 EndX=47.0149 EndY=-10 EndZ=0
    g7: Circle CenterX=47.0149 CenterY=-10 CenterZ=0 NormalX=0 NormalY=0 NormalZ=1 AngleXU=0 Radius=1.65
    g8: Circle CenterX=12.3667 CenterY=-44.6482 CenterZ=0 NormalX=0 NormalY=0 NormalZ=1 AngleXU=0 Radius=1.65
  constraints (20):
    c: Coincident(g0,g-4)
    c: Tangent(g1,g0) = -1.5708
    c: Coincident(g2,g1)
    c: Horizontal(g2)
    c: Coincident(g1,g-3)
    c: Tangent(g3,g2) = 1.5708
    c: Tangent(g5,g4) = 1.5708
    c: Tangent(g5,g3) = 1.5708
    c: Equal(g4,g3)
    c: Radius(g3) = 5
    c: Coincident(g6,g4)
    c: Coincident(g6,g3)
    c: Distance(g6) = 49
    c: Coincident(g7,g3)
    c: Coincident(g8,g4)
    c: Equal(g8,g7)
    c: Diameter(g7) = 3.3
    c: Tangent(g4,g0) = -1.5708
    c: Vertical(g0)
    c: Equal(g2,g0)
FEATURE [PartDesign::Pad] Pad008
  AddSubType = 0
  AutoTaperInnerAngle = true
  BaseFeature = -> Pocket007
  CheckUpToFaceLimits = true
  ClaimChildren = false
  Direction = (0,1,-4e-16)
  Fit = 0
  FitJoin = 0
  InnerFit = 0
  InnerFitJoin = 0
  InvalidShape = false
  Length = 3
  Length2 = 100
  NewSolid = false
  Profile = -> Sketch010
  Reversed = true
  Suppress = false
  TaperInnerAngle = 0
  TaperInnerAngleRev = 0
  TreeRank = 0
  Type = 0
  ValidateShape = true
  _ProfileBasedVersion = 0
FEATURE [Sketcher::SketchObject] Sketch020
  ArcFitTolerance = 0
  AttachmentSupport = -> [Pad008]
  ExternalBSplineMaxDegree = 0
  ExternalBSplineTolerance = 0
  FullyConstrained = false
  InternalTolerance = 1e-06
  InvalidShape = false
  MakeInternals = false
  MapMode = 5
  Placement = pos=(0,94,-5.73e-14) rot=(0,0.707107,0.707107;3.14159rad)
  Support = -> [Pad008]
  TreeRank = 0
  ValidateShape = false
  sketch-geometry (7):
    g0: LineSegment [constr] StartX=12.3667 StartY=-44.6482 StartZ=0 EndX=29.6908 EndY=-27.3241 EndZ=0
    g1: LineSegment [constr] StartX=47.0149 StartY=-10 StartZ=0 EndX=29.6908 EndY=-27.3241 EndZ=0
    g2: ArcOfCircle CenterX=29.6908 CenterY=-27.3241 CenterZ=0 NormalX=0 NormalY=0 NormalZ=1 AngleXU=0 Radius=7.5 StartAngle=1.85025 EndAngle=2.86214
    g3: LineSegment StartX=22.4817 StartY=-25.2554 StartZ=0 EndX=15.9022 EndY=-48.1838 EndZ=0
    g4: LineSegment StartX=27.6221 StartY=-20.1151 StartZ=0 EndX=50.5504 EndY=-13.5355 EndZ=0
    g5: LineSegment [constr] StartX=29.6908 StartY=-27.3241 StartZ=0 EndX=33.2263 EndY=-30.8597 EndZ=0
    g6: LineSegment StartX=15.9022 StartY=-48.1838 StartZ=0 EndX=50.5504 EndY=-13.5355 EndZ=0
  constraints (12):
    c: Coincident(g1,g0)
    c: Equal(g1,g0)
    c: Parallel(g1,g0)
    c: Coincident(g2,g0)
    c: Tangent(g4,g2) = 1.5708
    c: Tangent(g3,g2) = -1.5708
    c: Coincident(g5,g2)
    c: Perpendicular(g1,g5)
    c: Symmetric(g4,g3,g5)
    c: Radius(g2) = 7.5
    c: Coincident(g6,g3)
    c: Coincident(g6,g4)
FEATURE [PartDesign::Pocket] Pocket011
  AddSubType = 1
  AutoTaperInnerAngle = true
  BaseFeature = -> Pad008
  CheckUpToFaceLimits = true
  ClaimChildren = false
  Direction = (0,-1,7e-16)
  Fit = 0
  FitJoin = 0
  InnerFit = 0
  InnerFitJoin = 0
  InvalidShape = false
  Length = 5
  Length2 = 100
  NewSolid = false
  Profile = -> Sketch020
  Suppress = false
  TaperInnerAngle = 0
  TaperInnerAngleRev = 0
  TreeRank = 0
  Type = 1
  ValidateShape = true
  _ProfileBasedVersion = 0
  _Version = 0
FEATURE [PartDesign::Fillet] Fillet007
  AddSubType = 0
  Base = -> Pocket011 [Edge164,Edge178]
  BaseFeature = -> Pocket011
  InvalidShape = false
  NewSolid = false
  Radius = 4.5
  SupportTransform = true
  Suppress = false
  TreeRank = 0
  UseAllEdges = false
  ValidateShape = true
FEATURE [Sketcher::SketchObject] Sketch081
  ArcFitTolerance = 0
  AttachmentSupport = -> [Fillet007]
  ExternalBSplineMaxDegree = 0
  ExternalBSplineTolerance = 0
  FullyConstrained = true
  InternalTolerance = 1e-06
  InvalidShape = false
  MakeInternals = false
  MapMode = 5
  Placement = pos=(0,94,0) rot=(0,0.707107,0.707107;3.14159rad)
  Support = -> [Fillet007]
  TreeRank = 0
  ValidateShape = false
  sketch-geometry (4):
    g0: Circle CenterX=70 CenterY=2.5 CenterZ=0 NormalX=0 NormalY=0 NormalZ=1 AngleXU=0 Radius=2
    g1: Circle CenterX=132.5 CenterY=2.5 CenterZ=0 NormalX=0 NormalY=0 NormalZ=1 AngleXU=0 Radius=2
    g2: Circle CenterX=70 CenterY=2.5 CenterZ=0 NormalX=0 NormalY=0 NormalZ=1 AngleXU=0 Radius=4
    g3: Circle CenterX=132.5 CenterY=2.5 CenterZ=0 NormalX=0 NormalY=0 NormalZ=1 AngleXU=0 Radius=4
  constraints (10):
    c: DistanceX(g-1,g0) = 70
    c: DistanceX(g0,g1) = 62.5
    c: Equal(g1,g0)
    c: Diameter(g1) = 4
    c: DistanceY(g-1,g0) = 2.5
    c: Coincident(g2,g0)
    c: Coincident(g3,g1)
    c: Equal(g3,g2)
    c: Diameter(g3) = 8
    c: Horizontal(g1,g0)
FEATURE [PartDesign::Pad] Pad039
  AddSubType = 0
  AutoTaperInnerAngle = true
  BaseFeature = -> Fillet007
  CheckUpToFaceLimits = true
  ClaimChildren = false
  Direction = (0,1,-2e-16)
  Fit = 0
  FitJoin = 0
  InnerFit = 0
  InnerFitJoin = 0
  InvalidShape = false
  Length = 3
  Length2 = 100
  NewSolid = false
  Profile = -> Sketch081
  Suppress = false
  TaperInnerAngle = 0
  TaperInnerAngleRev = 0
  TreeRank = 0
  Type = 0
  ValidateShape = true
  _ProfileBasedVersion = 0
FEATURE [Sketcher::SketchObject] Sketch082
  ArcFitTolerance = 0
  AttachmentSupport = -> [Pad039]
  ExternalBSplineMaxDegree = 0
  ExternalBSplineTolerance = 0
  FullyConstrained = true
  InternalTolerance = 1e-06
  InvalidShape = false
  MakeInternals = false
  MapMode = 5
  Placement = pos=(0,94,0) rot=(0,0.707107,0.707107;3.14159rad)
  Support = -> [Pad039]
  TreeRank = 0
  ValidateShape = false
  sketch-geometry (2):
    g0: Circle CenterX=70 CenterY=2.5 CenterZ=0 NormalX=0 NormalY=0 NormalZ=1 AngleXU=0 Radius=2
    g1: Circle CenterX=132.5 CenterY=2.5 CenterZ=0 NormalX=0 NormalY=0 NormalZ=1 AngleXU=0 Radius=2
  constraints (6):
    c: Equal(g0,g1)
    c: Diameter(g1) = 4
    c: DistanceX(g0,g1) = 62.5
    c: DistanceX(g-1,g0) = 70
    c: DistanceY(g-1,g0) = 2.5
    c: Horizontal(g0,g1)
FEATURE [PartDesign::Pocket] Pocket045
  AddSubType = 1
  AutoTaperInnerAngle = true
  BaseFeature = -> Pad039
  CheckUpToFaceLimits = true
  ClaimChildren = false
  Direction = (0,-1,2e-16)
  Fit = 0
  FitJoin = 0
  InnerFit = 0
  InnerFitJoin = 0
  InvalidShape = false
  Length = 3
  Length2 = 100
  NewSolid = false
  Profile = -> Sketch082
  Suppress = false
  TaperInnerAngle = 0
  TaperInnerAngleRev = 0
  TreeRank = 0
  Type = 0
  ValidateShape = true
  _ProfileBasedVersion = 0
  _Version = 0
FEATURE [PartDesign::Chamfer] Chamfer030
  AddSubType = 0
  Angle = 45
  Base = -> Pocket045 [Edge65,Edge67]
  BaseFeature = -> Pocket045
  ChamferType = 0
  FlipDirection = false
  InvalidShape = false
  NewSolid = false
  Size = 2.9
  Size2 = 1
  SupportTransform = true
  Suppress = false
  TreeRank = 0
  UseAllEdges = false
  ValidateShape = true
FEATURE [PartDesign::Fillet] Fillet022
  AddSubType = 0
  Base = -> Chamfer030 [Edge25]
  BaseFeature = -> Chamfer030
  InvalidShape = false
  NewSolid = false
  Radius = 1.5
  SupportTransform = true
  Suppress = false
  TreeRank = 0
  UseAllEdges = false
  ValidateShape = true
FEATURE [PartDesign::Body] Body001
  AutoGroupSolids = false
  ClaimAllChildren = false
  ExportMode = 0
  Group = -> [Sketch018,Pad007,Pad006,Sketch017,Pad005,Mirrored003,Fillet006,Sketch016,Pad003,Mirrored002,Chamfer002,Sketch015,Pocket010,Sketch014,Pad004,Sketch013,Pocket009,Chamfer003,Sketch012,Pocket008,Sketch011,Pocket003,Pocket004,Sketch009,Pocket005,Pocket006,Pocket007,Sketch010,Pad008,Sketch020,Pocket011,Fillet007,Sketch081,Pad039,Sketch082,Pocket045,Chamfer030,Fillet022]
  InvalidShape = false
  Origin = -> Origin001
  SingleSolid = true
  Tip = -> Fillet022
  TreeRank = 0
  ValidateShape = false
  _ExportChildren = -> [Pad007,Pad006,Pad005,Mirrored003,Fillet006,Pad003,Mirrored002,Chamfer002,Pocket010,Pad004,Pocket009,Chamfer003,Pocket008,Pocket003,Pocket004,Pocket005,Pocket006,Pocket007,Pad008,Pocket011,Fillet007,Pad039,Pocket045,Chamfer030,Fillet022]
  _GroupVersion = 1
COMPONENT P2 — recipe-attached ("Body002", modeled in this document).
Construction recipe (the document's own serialized feature program — sketch geometry with constraints, then the solid features built on it; lengths are millimeters unless a unit is written):

FEATURE [Sketcher::SketchObject] Sketch026
  ArcFitTolerance = 0
  AttachmentSupport = -> [XY_Plane002]
  ExternalBSplineMaxDegree = 0
  ExternalBSplineTolerance = 0
  FullyConstrained = false
  InternalTolerance = 1e-06
  InvalidShape = false
  MakeInternals = false
  MapMode = 5
  Support = -> [XY_Plane002]
  TreeRank = 0
  ValidateShape = false
  sketch-geometry (1):
    g0: Circle CenterX=0 CenterY=0 CenterZ=0 NormalX=0 NormalY=0 NormalZ=1 AngleXU=0 Radius=21
  constraints (2):
    c: Coincident(g0,g-1)
    c: Diameter(g0) = 42
FEATURE [PartDesign::Pad] Pad015
  AddSubType = 0
  AutoTaperInnerAngle = true
  CheckUpToFaceLimits = true
  ClaimChildren = false
  Direction = (1,1,1)
  Fit = 0
  FitJoin = 0
  InnerFit = 0
  InnerFitJoin = 0
  InvalidShape = false
  Length = 22.25
  Length2 = 100
  Midplane = true
  NewSolid = false
  Profile = -> Sketch026
  Suppress = false
  TaperInnerAngle = 0
  TaperInnerAngleRev = 0
  TreeRank = 0
  Type = 0
  ValidateShape = true
  _ProfileBasedVersion = 0
FEATURE [Sketcher::SketchObject] Sketch027
  ArcFitTolerance = 0
  AttachmentSupport = -> [Pad015]
  ExternalBSplineMaxDegree = 0
  ExternalBSplineTolerance = 0
  FullyConstrained = false
  InternalTolerance = 1e-06
  InvalidShape = false
  MakeInternals = false
  MapMode = 5
  Placement = pos=(0,0,-11.125) rot=(1,0,0;3.14159rad)
  Support = -> [Pad015]
  TreeRank = 0
  ValidateShape = false
  sketch-geometry (1):
    g0: Circle CenterX=0 CenterY=0 CenterZ=0 NormalX=0 NormalY=0 NormalZ=1 AngleXU=0 Radius=4.95
  constraints (2):
    c: Coincident(g0,g-1)
    c: Diameter(g0) = 9.9
FEATURE [PartDesign::Pad] Pad016
  AddSubType = 0
  AutoTaperInnerAngle = true
  BaseFeature = -> Pad015
  CheckUpToFaceLimits = true
  ClaimChildren = false
  Direction = (1,1,1)
  Fit = 0
  FitJoin = 0
  InnerFit = 0
  InnerFitJoin = 0
  InvalidShape = false
  Length = 1.5
  Length2 = 100
  NewSolid = false
  Profile = -> Sketch027
  Suppress = false
  TaperInnerAngle = 0
  TaperInnerAngleRev = 0
  TreeRank = 0
  Type = 0
  ValidateShape = true
  _ProfileBasedVersion = 0
FEATURE [Sketcher::SketchObject] Sketch028
  ArcFitTolerance = 0
  AttachmentSupport = -> [Plane003]
  ExternalBSplineMaxDegree = 0
  ExternalBSplineTolerance = 0
  ExternalGeometry = -> [Pad016]
  FullyConstrained = false
  InternalTolerance = 1e-06
  InvalidShape = false
  MakeInternals = false
  MapMode = 5
  Placement = pos=(0,0,-8.73) rot=(1,0,0;3.14159rad)
  Support = -> [Plane003]
  TreeRank = 0
  ValidateShape = false
  sketch-geometry (5):
    g0: ArcOfCircle CenterX=0 CenterY=0 CenterZ=0 NormalX=0 NormalY=0 NormalZ=1 AngleXU=0 Radius=21 StartAngle=1.26361 EndAngle=1.87799
    g1: LineSegment StartX=-6.35 StartY=20.0169 StartZ=0 EndX=-6.35 EndY=26.5 EndZ=0
    g2: LineSegment StartX=-6.35 StartY=26.5 StartZ=0 EndX=6.35 EndY=26.5 EndZ=0
    g3: LineSegment StartX=6.35 StartY=26.5 StartZ=0 EndX=6.35 EndY=20.0169 EndZ=0
    g4: LineSegment [constr] StartX=0 StartY=26.5 StartZ=0 EndX=0 EndY=21 EndZ=0
  constraints (16):
    c: Coincident(g0,g-1)
    c: PointOnObject(g0,g-3)
    c: Coincident(g0,g1)
    c: Coincident(g1,g2)
    c: Horizontal(g2)
    c: Coincident(g2,g3)
    c: Coincident(g3,g0)
    c: Vertical(g3)
    c: Symmetric(g0,g0,g-2)
    c: Vertical(g1)
    c: DistanceX(g2,g2) = 12.7
    c: PointOnObject(g4,g-2)
    c: PointOnObject(g4,g0)
    c: PointOnObject(g4,g-2)
    c: PointOnObject(g4,g2)
    c: DistanceY(g4,g4) = 5.5
FEATURE [PartDesign::Pad] Pad009
  AddSubType = 0
  AutoTaperInnerAngle = true
  BaseFeature = -> Pad016
  CheckUpToFaceLimits = true
  ClaimChildren = false
  Direction = (1,1,1)
  Fit = 0
  FitJoin = 0
  InnerFit = 0
  InnerFitJoin = 0
  InvalidShape = false
  Length = 11.8
  Length2 = 100
  NewSolid = false
  Profile = -> Sketch028
  Reversed = true
  Suppress = false
  TaperInnerAngle = 0
  TaperInnerAngleRev = 0
  TreeRank = 0
  Type = 0
  ValidateShape = true
  _ProfileBasedVersion = 0
FEATURE [Sketcher::SketchObject] Sketch021
  ArcFitTolerance = 0
  AttachmentSupport = -> [Pad009]
  ExternalBSplineMaxDegree = 0
  ExternalBSplineTolerance = 0
  ExternalGeometry = -> [Pad009]
  FullyConstrained = false
  InternalTolerance = 1e-06
  InvalidShape = false
  MakeInternals = false
  MapMode = 5
  Placement = pos=(0,9e-16,3.07) rot=(0,0,1;0rad)
  Support = -> [Pad009]
  TreeRank = 0
  ValidateShape = false
  sketch-geometry (4):
    g0: ArcOfCircle CenterX=-4.3e-15 CenterY=-1e-16 CenterZ=0 NormalX=0 NormalY=0 NormalZ=1 AngleXU=0 Radius=21 StartAngle=4.4052 EndAngle=5.01958
    g1: ArcOfCircle CenterX=-4.3e-15 CenterY=-1e-16 CenterZ=0 NormalX=0 NormalY=0 NormalZ=1 AngleXU=0 Radius=21.7161 StartAngle=4.41564 EndAngle=5.00914
    g2: LineSegment StartX=-6.35 StartY=-20.0169 StartZ=0 EndX=-6.35 EndY=-20.7669 EndZ=0
    g3: LineSegment StartX=6.35 StartY=-20.0169 StartZ=0 EndX=6.35 EndY=-20.7669 EndZ=0
  constraints (11):
    c: Coincident(g0,g-3)
    c: Coincident(g0,g-3)
    c: Equal(g-3,g0)
    c: Coincident(g1,g0)
    c: Coincident(g2,g0)
    c: Vertical(g2)
    c: Coincident(g3,g0)
    c: Vertical(g3)
    c: Coincident(g1,g2)
    c: Coincident(g3,g1)
    c: DistanceY(g3,g3) = 0.75
FEATURE [PartDesign::Pad] Pad010
  AddSubType = 0
  AutoTaperInnerAngle = true
  BaseFeature = -> Pad009
  CheckUpToFaceLimits = true
  ClaimChildren = false
  Direction = (1,1,1)
  Fit = 0
  FitJoin = 0
  InnerFit = 0
  InnerFitJoin = 0
  InvalidShape = false
  Length = 2.2
  Length2 = 100
  NewSolid = false
  Profile = -> Sketch021
  Suppress = false
  TaperInnerAngle = 0
  TaperInnerAngleRev = 0
  TreeRank = 0
  Type = 0
  ValidateShape = true
  _ProfileBasedVersion = 0
FEATURE [Sketcher::SketchObject] Sketch022
  ArcFitTolerance = 0
  AttachmentSupport = -> [Pad010]
  ExternalBSplineMaxDegree = 0
  ExternalBSplineTolerance = 0
  ExternalGeometry = -> [Pad010]
  FullyConstrained = false
  InternalTolerance = 1e-06
  InvalidShape = false
  MakeInternals = false
  MapMode = 5
  Placement = pos=(0,0,11.125) rot=(0,0,1;0rad)
  Support = -> [Pad010]
  TreeRank = 0
  ValidateShape = false
  sketch-geometry (12):
    g0: Circle CenterX=24.5 CenterY=0 CenterZ=0 NormalX=0 NormalY=0 NormalZ=1 AngleXU=0 Radius=1.5
    g1: ArcOfCircle CenterX=24.5 CenterY=0 CenterZ=0 NormalX=0 NormalY=0 NormalZ=1 AngleXU=0 Radius=4.25 StartAngle=5.46517 EndAngle=7.1012
    g2: LineSegment StartX=27.4056 StartY=3.1016 StartZ=0 EndX=14.3571 EndY=15.3255 EndZ=0
    g3: LineSegment StartX=27.4056 StartY=-3.1016 StartZ=0 EndX=14.3571 EndY=-15.3255 EndZ=0
    g4: Circle CenterX=-24.5 CenterY=0 CenterZ=0 NormalX=0 NormalY=0 NormalZ=1 AngleXU=0 Radius=1.5
    g5: ArcOfCircle CenterX=-24.5 CenterY=0 CenterZ=0 NormalX=0 NormalY=0 NormalZ=1 AngleXU=0 Radius=4.25 StartAngle=2.32358 EndAngle=3.9596
    g6: LineSegment StartX=-27.4056 StartY=-3.1016 StartZ=0 EndX=-14.3571 EndY=-15.3256 EndZ=0
    g7: LineSegment StartX=-27.4056 StartY=3.1016 StartZ=0 EndX=-14.3571 EndY=15.3255 EndZ=0
    g8: GeomPoint [constr] X=-28.75 Y=0 Z=0
    g9: GeomPoint [constr] X=28.75 Y=0 Z=0
    g10: ArcOfCircle CenterX=2.3e-15 CenterY=-1.1e-15 CenterZ=0 NormalX=0 NormalY=0 NormalZ=1 AngleXU=0 Radius=21 StartAngle=2.32358 EndAngle=3.95961
    g11: ArcOfCircle CenterX=4e-16 CenterY=-1.3e-15 CenterZ=0 NormalX=0 NormalY=0 NormalZ=1 AngleXU=0 Radius=21 StartAngle=5.46517 EndAngle=7.1012
  constraints (30):
    c: PointOnObject(g0,g-1)
    c: Coincident(g1,g0)
    c: Diameter(g0) = 3
    c: PointOnObject(g2,g-3)
    c: PointOnObject(g3,g-3)
    c: Tangent(g2,g-3)
    c: Tangent(g3,g-3)
    c: Coincident(g5,g4)
    c: PointOnObject(g7,g-3)
    c: PointOnObject(g6,g-3)
    c: Tangent(g7,g-3)
    c: Tangent(g7,g5) = 1.5708
    c: Tangent(g6,g5) = -1.5708
    c: Equal(g4,g0)
    c: Symmetric(g4,g0,g-2)
    c: Tangent(g2,g1) = -1.5708
    c: Tangent(g3,g1) = 1.5708
    c: DistanceX(g4,g0) = 49
    c: Symmetric(g5,g1,g-2)
    c: PointOnObject(g8,g-1)
    c: PointOnObject(g8,g5)
    c: PointOnObject(g9,g-1)
    c: PointOnObject(g9,g1)
    c: DistanceX(g8,g9) = 57.5
    c: Coincident(g10,g7)
    c: Coincident(g10,g6)
    c: Equal(g10,g-3)
    c: Coincident(g11,g2)
    c: Coincident(g11,g3)
    c: Equal(g11,g-3)
FEATURE [PartDesign::Pad] Pad011
  AddSubType = 0
  AutoTaperInnerAngle = true
  BaseFeature = -> Pad010
  CheckUpToFaceLimits = true
  ClaimChildren = false
  Direction = (1,1,1)
  Fit = 0
  FitJoin = 0
  InnerFit = 0
  InnerFitJoin = 0
  InvalidShape = false
  Length = 1
  Length2 = 100
  NewSolid = false
  Profile = -> Sketch022
  Reversed = true
  Suppress = false
  TaperInnerAngle = 0
  TaperInnerAngleRev = 0
  TreeRank = 0
  Type = 0
  ValidateShape = true
  _ProfileBasedVersion = 0
FEATURE [Sketcher::SketchObject] Sketch023
  ArcFitTolerance = 0
  AttachmentSupport = -> [Pad011]
  ExternalBSplineMaxDegree = 0
  ExternalBSplineTolerance = 0
  ExternalGeometry = -> [Pad011]
  FullyConstrained = false
  InternalTolerance = 1e-06
  InvalidShape = false
  MakeInternals = false
  MapMode = 5
  Placement = pos=(0,0,11.125) rot=(0,0,1;0rad)
  Support = -> [Pad011]
  TreeRank = 0
  ValidateShape = false
  sketch-geometry (1):
    g0: Circle CenterX=0 CenterY=0 CenterZ=0 NormalX=0 NormalY=0 NormalZ=1 AngleXU=0 Radius=4.95
  constraints (2):
    c: Coincident(g0,g-1)
    c: Equal(g-3,g0)
FEATURE [PartDesign::Pad] Pad012
  AddSubType = 0
  AutoTaperInnerAngle = true
  BaseFeature = -> Pad011
  CheckUpToFaceLimits = true
  ClaimChildren = false
  Direction = (1,1,1)
  Fit = 0
  FitJoin = 0
  InnerFit = 0
  InnerFitJoin = 0
  InvalidShape = false
  Length = 1.5
  Length2 = 100
  NewSolid = false
  Profile = -> Sketch023
  Suppress = false
  TaperInnerAngle = 0
  TaperInnerAngleRev = 0
  TreeRank = 0
  Type = 0
  ValidateShape = true
  _ProfileBasedVersion = 0
FEATURE [Sketcher::SketchObject] Sketch024
  ArcFitTolerance = 0
  AttachmentSupport = -> [Pad012]
  ExternalBSplineMaxDegree = 0
  ExternalBSplineTolerance = 0
  FullyConstrained = false
  InternalTolerance = 1e-06
  InvalidShape = false
  MakeInternals = false
  MapMode = 5
  Placement = pos=(0,0,12.625) rot=(0,0,1;0rad)
  Support = -> [Pad012]
  TreeRank = 0
  ValidateShape = false
  sketch-geometry (1):
    g0: Circle CenterX=0 CenterY=0 CenterZ=0 NormalX=0 NormalY=0 NormalZ=1 AngleXU=0 Radius=1.5
  constraints (2):
    c: Coincident(g0,g-1)
    c: Diameter(g0) = 3
FEATURE [PartDesign::Pad] Pad013
  AddSubType = 0
  AutoTaperInnerAngle = true
  BaseFeature = -> Pad012
  CheckUpToFaceLimits = true
  ClaimChildren = false
  Direction = (1,1,1)
  Fit = 0
  FitJoin = 0
  InnerFit = 0
  InnerFitJoin = 0
  InvalidShape = false
  Length = 2
  Length2 = 100
  NewSolid = false
  Profile = -> Sketch024
  Suppress = false
  TaperInnerAngle = 0
  TaperInnerAngleRev = 0
  TreeRank = 0
  Type = 0
  ValidateShape = true
  _ProfileBasedVersion = 0
FEATURE [PartDesign::Pad] Pad014
  AddSubType = 0
  AutoTaperInnerAngle = true
  BaseFeature = -> Pad013
  CheckUpToFaceLimits = true
  ClaimChildren = false
  Direction = (1,1,1)
  Fit = 0
  FitJoin = 0
  InnerFit = 0
  InnerFitJoin = 0
  InvalidShape = false
  Length = 8
  Length2 = 100
  NewSolid = false
  Profile = -> InvoluteGear
  Suppress = false
  TaperInnerAngle = 0
  TaperInnerAngleRev = 0
  TreeRank = 0
  Type = 0
  ValidateShape = true
  _ProfileBasedVersion = 0
FEATURE [Sketcher::SketchObject] Sketch025
  ArcFitTolerance = 0
  AttachmentSupport = -> [Pad013]
  ExternalBSplineMaxDegree = 0
  ExternalBSplineTolerance = 0
  FullyConstrained = true
  InternalTolerance = 1e-06
  InvalidShape = false
  MakeInternals = false
  MapMode = 5
  Placement = pos=(0,0,14.625) rot=(0,0,1;0rad)
  Support = -> [Pad013]
  TreeRank = 0
  ValidateShape = false
FEATURE [PartDesign::Body] Body002
  AutoGroupSolids = false
  ClaimAllChildren = false
  ExportMode = 0
  Group = -> [Sketch026,Pad015,Sketch027,Pad016,Sketch028,Pad009,Sketch021,Pad010,Sketch022,Pad011,Sketch023,Pad012,Sketch024,Pad013,Sketch025,Pad014]
  InvalidShape = false
  Origin = -> Origin002
  SingleSolid = true
  Tip = -> Pad014
  TreeRank = 0
  ValidateShape = false
  _ExportChildren = -> [Pad015,Pad016,Pad009,Pad010,Pad011,Pad012,Pad013,Sketch025,Pad014]
  _GroupVersion = 1
COMPONENT P3 — recipe-attached ("Body003", modeled in this document).
Construction recipe (the document's own serialized feature program — sketch geometry with constraints, then the solid features built on it; lengths are millimeters unless a unit is written):

FEATURE [Sketcher::SketchObject] Sketch029
  ArcFitTolerance = 0
  AttachmentSupport = -> [XY_Plane003]
  ExternalBSplineMaxDegree = 0
  ExternalBSplineTolerance = 0
  FullyConstrained = false
  InternalTolerance = 1e-06
  InvalidShape = false
  MakeInternals = false
  MapMode = 5
  Support = -> [XY_Plane003]
  TreeRank = 0
  ValidateShape = false
  sketch-geometry (1):
    g0: Circle CenterX=0 CenterY=0 CenterZ=0 NormalX=0 NormalY=0 NormalZ=1 AngleXU=0 Radius=15
  constraints (2):
    c: Coincident(g0,g-1)
    c: Diameter(g0) = 30
FEATURE [PartDesign::Pad] Pad017
  AddSubType = 0
  AutoTaperInnerAngle = true
  CheckUpToFaceLimits = true
  ClaimChildren = false
  Direction = (1,1,1)
  Fit = 0
  FitJoin = 0
  InnerFit = 0
  InnerFitJoin = 0
  InvalidShape = false
  Length = 8
  Length2 = 100
  NewSolid = false
  Profile = -> Sketch029
  Suppress = false
  TaperInnerAngle = 0
  TaperInnerAngleRev = 0
  TreeRank = 0
  Type = 0
  ValidateShape = true
  _ProfileBasedVersion = 0
FEATURE [Sketcher::SketchObject] Sketch030
  ArcFitTolerance = 0
  AttachmentSupport = -> [Pad017]
  ExternalBSplineMaxDegree = 0
  ExternalBSplineTolerance = 0
  FullyConstrained = false
  InternalTolerance = 1e-06
  InvalidShape = false
  MakeInternals = false
  MapMode = 5
  Placement = pos=(0,0,8) rot=(0,0,1;0rad)
  Support = -> [Pad017]
  TreeRank = 0
  ValidateShape = false
  sketch-geometry (1):
    g0: Circle CenterX=0 CenterY=0 CenterZ=0 NormalX=0 NormalY=0 NormalZ=1 AngleXU=0 Radius=2
  constraints (2):
    c: Coincident(g0,g-1)
    c: Diameter(g0) = 4
FEATURE [PartDesign::Pocket] Pocket012
  AddSubType = 1
  AutoTaperInnerAngle = true
  BaseFeature = -> Pad017
  CheckUpToFaceLimits = true
  ClaimChildren = false
  Direction = (1,1,1)
  Fit = 0
  FitJoin = 0
  InnerFit = 0
  InnerFitJoin = 0
  InvalidShape = false
  Length = 6
  Length2 = 100
  NewSolid = false
  Profile = -> Sketch030
  Suppress = false
  TaperInnerAngle = 0
  TaperInnerAngleRev = 0
  TreeRank = 0
  Type = 0
  ValidateShape = true
  _ProfileBasedVersion = 0
  _Version = 0
FEATURE [PartDesign::SubShapeBinder] Binder
  BindCopyOnChange = 0
  BindMode = 0
  ClaimChildren = false
  Context = -> Assembly002 [Parts002.Assembly004.Parts004.Body003.Binder.]
  EdgeTolerance = 1e-06
  FillStyle = 0
  Fuse = false
  InvalidShape = false
  MakeFace = true
  MergeEdges = true
  OffsetFill = false
  OffsetIntersection = false
  OffsetJoinType = 0
  OffsetOpenResult = false
  Outline = false
  PartialLoad = false
  Refine = true
  Relative = true
  SplitEdges = false
  Support = -> [Assembly003[Parts003.Body002.Pad014.Face201]]
  TightBound = false
  TreeRank = 0
  ValidateShape = false
  _Version = 3
FEATURE [PartDesign::Pocket] Pocket013
  AddSubType = 1
  AutoTaperInnerAngle = true
  BaseFeature = -> Pocket012
  CheckUpToFaceLimits = true
  ClaimChildren = false
  Direction = (3.89386e-08,-1.84716e-07,1)
  Fit = 0
  FitJoin = 0
  InnerFit = 0
  InnerFitJoin = 0
  InvalidShape = false
  Length = 5
  Length2 = 100
  NewSolid = false
  Profile = -> Binder
  Suppress = false
  TaperInnerAngle = 0
  TaperInnerAngleRev = 0
  TreeRank = 0
  Type = 1
  ValidateShape = true
  _ProfileBasedVersion = 0
  _Version = 0
FEATURE [PartDesign::Body] Body003
  AutoGroupSolids = false
  ClaimAllChildren = false
  ExportMode = 0
  Group = -> [Sketch029,Pad017,Sketch030,Pocket012,Binder,Pocket013]
  InvalidShape = false
  Origin = -> Origin003
  SingleSolid = true
  Tip = -> Pocket013
  TreeRank = 0
  ValidateShape = false
  _ExportChildren = -> [Pad017,Pocket012,Pocket013]
  _GroupVersion = 1
COMPONENT P4 — recipe-attached ("Body004", modeled in this document).
Construction recipe (the document's own serialized feature program — sketch geometry with constraints, then the solid features built on it; lengths are millimeters unless a unit is written):

FEATURE [Sketcher::SketchObject] Sketch031
  ArcFitTolerance = 0
  AttachmentSupport = -> [XY_Plane004]
  ExternalBSplineMaxDegree = 0
  ExternalBSplineTolerance = 0
  FullyConstrained = false
  InternalTolerance = 1e-06
  InvalidShape = false
  MakeInternals = false
  MapMode = 5
  Support = -> [XY_Plane004]
  TreeRank = 0
  ValidateShape = false
  sketch-geometry (16):
    g0: LineSegment StartX=-154 StartY=89 StartZ=0 EndX=154 EndY=89 EndZ=0
    g1: LineSegment StartX=164 StartY=79 StartZ=0 EndX=164 EndY=-79 EndZ=0
    g2: LineSegment StartX=154 StartY=-89 StartZ=0 EndX=-154 EndY=-89 EndZ=0
    g3: LineSegment StartX=-164 StartY=-79 StartZ=0 EndX=-164 EndY=79 EndZ=0
    g4: ArcOfCircle CenterX=-154 CenterY=79 CenterZ=0 NormalX=0 NormalY=0 NormalZ=1 AngleXU=0 Radius=10 StartAngle=1.5708 EndAngle=3.14159
    g5: ArcOfCircle CenterX=154 CenterY=79 CenterZ=0 NormalX=0 NormalY=0 NormalZ=1 AngleXU=0 Radius=10 StartAngle=-9e-16 EndAngle=1.5708
    g6: ArcOfCircle CenterX=154 CenterY=-79 CenterZ=0 NormalX=0 NormalY=0 NormalZ=1 AngleXU=0 Radius=10 StartAngle=4.71239 EndAngle=6.28319
    g7: ArcOfCircle CenterX=-154 CenterY=-79 CenterZ=0 NormalX=0 NormalY=0 NormalZ=1 AngleXU=0 Radius=10 StartAngle=3.14159 EndAngle=4.71239
    g8: LineSegment StartX=-154 StartY=94 StartZ=0 EndX=154 EndY=94 EndZ=0
    g9: LineSegment StartX=169 StartY=79 StartZ=0 EndX=169 EndY=-79 EndZ=0
    g10: LineSegment StartX=154 StartY=-94 StartZ=0 EndX=-154 EndY=-94 EndZ=0
    g11: LineSegment StartX=-169 StartY=-79 StartZ=0 EndX=-169 EndY=79 EndZ=0
    g12: ArcOfCircle CenterX=-154 CenterY=79 CenterZ=0 NormalX=0 NormalY=0 NormalZ=1 AngleXU=0 Radius=15 StartAngle=1.5708 EndAngle=3.14159
    g13: ArcOfCircle CenterX=154 CenterY=79 CenterZ=0 NormalX=0 NormalY=0 NormalZ=1 AngleXU=0 Radius=15 StartAngle=1e-16 EndAngle=1.5708
    g14: ArcOfCircle CenterX=154 CenterY=-79 CenterZ=0 NormalX=0 NormalY=0 NormalZ=1 AngleXU=0 Radius=15 StartAngle=4.71239 EndAngle=6.28319
    g15: ArcOfCircle CenterX=-154 CenterY=-79 CenterZ=0 NormalX=0 NormalY=0 NormalZ=1 AngleXU=0 Radius=15 StartAngle=3.14159 EndAngle=4.71239
  constraints (35):
    c: Tangent(g3,g4) = 1.5708
    c: Tangent(g0,g4) = 1.5708
    c: Tangent(g0,g5) = 1.5708
    c: Tangent(g1,g5) = 1.5708
    c: Tangent(g1,g6) = 1.5708
    c: Tangent(g2,g6) = 1.5708
    c: Tangent(g2,g7) = 1.5708
    c: Tangent(g3,g7) = 1.5708
    c: Equal(g5,g6)
    c: Equal(g6,g7)
    c: Equal(g7,g4)
    c: Symmetric(g3,g1,g-2)
    c: Symmetric(g3,g1,g-2)
    c: Symmetric(g3,g3,g-1)
    c: DistanceX(g3,g1) = 328
    c: DistanceY(g2,g0) = 178
    c: Radius(g5) = 10
    c: Tangent(g11,g12) = 1.5708
    c: Tangent(g8,g12) = 1.5708
    c: Tangent(g8,g13) = 1.5708
    c: Tangent(g9,g13) = 1.5708
    c: Tangent(g9,g14) = 1.5708
    c: Tangent(g10,g14) = 1.5708
    c: Tangent(g10,g15) = 1.5708
    c: Tangent(g11,g15) = 1.5708
    c: Horizontal(g8)
    c: Horizontal(g10)
    c: Vertical(g9)
    c: Vertical(g11)
    c: DistanceX(g11,g3) = 5
    c: DistanceY(g0,g8) = 5
    c: Equal(g14,g13)
    c: Equal(g13,g12)
    c: Coincident(g15,g7)
    c: Coincident(g13,g5)
FEATURE [PartDesign::Pad] Pad018
  AddSubType = 0
  AutoTaperInnerAngle = true
  CheckUpToFaceLimits = true
  ClaimChildren = false
  Direction = (1,1,1)
  Fit = 0
  FitJoin = 0
  InnerFit = 0
  InnerFitJoin = 0
  InvalidShape = false
  Length = 10
  Length2 = 100
  NewSolid = false
  Profile = -> Sketch031
  Suppress = false
  TaperInnerAngle = 0
  TaperInnerAngleRev = 0
  TreeRank = 0
  Type = 0
  ValidateShape = true
  _ProfileBasedVersion = 0
FEATURE [PartDesign::Pad] Pad019
  AddSubType = 0
  AutoTaperInnerAngle = true
  BaseFeature = -> Pad018
  CheckUpToFaceLimits = true
  ClaimChildren = false
  Direction = (1,1,1)
  Fit = 0
  FitJoin = 0
  InnerFit = 0
  InnerFitJoin = 0
  InvalidShape = false
  Length = 5
  Length2 = 100
  NewSolid = false
  Profile = -> Sketch032
  Reversed = true
  Suppress = false
  TaperInnerAngle = 0
  TaperInnerAngleRev = 0
  TreeRank = 0
  Type = 0
  ValidateShape = true
  _ProfileBasedVersion = 0
FEATURE [Sketcher::SketchObject] Sketch033
  ArcFitTolerance = 0
  AttachmentSupport = -> [Pad019]
  ExternalBSplineMaxDegree = 0
  ExternalBSplineTolerance = 0
  ExternalGeometry = -> [Pad019]
  FullyConstrained = false
  InternalTolerance = 1e-06
  InvalidShape = false
  MakeInternals = false
  MapMode = 5
  Placement = pos=(0,94,0) rot=(0,0.707107,0.707107;3.14159rad)
  Support = -> [Pad019]
  TreeRank = 0
  ValidateShape = false
  sketch-geometry (6):
    g0: LineSegment StartX=-7.36667 StartY=-5 StartZ=0 EndX=7.36667 EndY=-5 EndZ=0
    g1: LineSegment StartX=-7.36667 StartY=-5 StartZ=0 EndX=-7.36667 EndY=-45 EndZ=0
    g2: LineSegment StartX=7.36667 StartY=-45 StartZ=0 EndX=7.36667 EndY=-5 EndZ=0
    g3: ArcOfCircle CenterX=5.36667 CenterY=-45 CenterZ=0 NormalX=0 NormalY=0 NormalZ=1 AngleXU=0 Radius=2 StartAngle=2.77438 EndAngle=6.28319
    g4: ArcOfCircle CenterX=-1e-16 CenterY=-42.9357 CenterZ=0 NormalX=0 NormalY=0 NormalZ=1 AngleXU=0 Radius=3.75 StartAngle=5.91598 EndAngle=9.79199
    g5: ArcOfCircle CenterX=-5.36667 CenterY=-45 CenterZ=0 NormalX=0 NormalY=0 NormalZ=1 AngleXU=0 Radius=2 StartAngle=3.14159 EndAngle=6.65039
  constraints (15):
    c: Symmetric(g0,g0,g-2)
    c: Coincident(g1,g0)
    c: Vertical(g1)
    c: Coincident(g2,g0)
    c: PointOnObject(g0,g-4)
    c: Symmetric(g2,g1,g-2)
    c: Tangent(g3,g2) = -1.5708
    c: Coincident(g5,g4)
    c: Tangent(g1,g5) = -1.5708
    c: Symmetric(g3,g4,g-2)
    c: Tangent(g4,g3) = 1.5708
    c: Diameter(g4) = 7.5
    c: Radius(g3) = 2
    c: DistanceX(g4,g3) = 7
    c: DistanceY(g1,g1) = 40
FEATURE [PartDesign::Pad] Pad020
  AddSubType = 0
  AutoTaperInnerAngle = true
  BaseFeature = -> Pad019
  CheckUpToFaceLimits = true
  ClaimChildren = false
  Direction = (1,1,1)
  Fit = 0
  FitJoin = 0
  InnerFit = 0
  InnerFitJoin = 0
  InvalidShape = false
  Length = 10
  Length2 = 100
  NewSolid = false
  Profile = -> Sketch033
  Reversed = true
  Suppress = false
  TaperInnerAngle = 0
  TaperInnerAngleRev = 0
  TreeRank = 0
  Type = 3
  UpToFace = -> Pad019 [Face27]
  ValidateShape = true
  _ProfileBasedVersion = 0
FEATURE [PartDesign::Mirrored] Mirrored004
  AddSubType = 0
  BaseFeature = -> Pad020
  CopyShape = true
  InvalidShape = false
  MirrorPlane = -> XZ_Plane004
  NewSolid = false
  OriginalSubs = -> [Pad020]
  Originals = -> [Pad020]
  ParallelTransform = true
  SubTransform = true
  Suppress = false
  TreeRank = 0
  ValidateShape = true
  _Version = 0
FEATURE [PartDesign::Fillet] Fillet008
  AddSubType = 0
  Base = -> Mirrored004 [Edge100,Edge42,Edge36,Edge104]
  BaseFeature = -> Mirrored004
  InvalidShape = false
  NewSolid = false
  Radius = 10
  SupportTransform = true
  Suppress = false
  TreeRank = 0
  UseAllEdges = false
  ValidateShape = true
FEATURE [Sketcher::SketchObject] Sketch035
  ArcFitTolerance = 0
  ExternalBSplineMaxDegree = 0
  ExternalBSplineTolerance = 0
  FullyConstrained = false
  InternalTolerance = 1e-06
  InvalidShape = false
  MakeInternals = false
  MapMode = 5
  Placement = pos=(0,0,10) rot=(0,0,1;0rad)
  TreeRank = 0
  ValidateShape = false
  sketch-geometry (4):
    g0: LineSegment StartX=0 StartY=119.45 StartZ=0 EndX=0 EndY=-119.45 EndZ=0
    g1: LineSegment StartX=0 StartY=119.45 StartZ=0 EndX=200.233 EndY=119.45 EndZ=0
    g2: LineSegment StartX=200.233 StartY=119.45 StartZ=0 EndX=200.233 EndY=-119.45 EndZ=0
    g3: LineSegment StartX=200.233 StartY=-119.45 StartZ=0 EndX=0 EndY=-119.45 EndZ=0
  constraints (9):
    c: PointOnObject(g0,g-2)
    c: Symmetric(g0,g0,g-1)
    c: Coincident(g0,g1)
    c: Horizontal(g1)
    c: Coincident(g1,g2)
    c: Vertical(g2)
    c: Coincident(g2,g3)
    c: Coincident(g3,g0)
    c: Horizontal(g3)
FEATURE [Sketcher::SketchObject] Sketch034
  ArcFitTolerance = 0
  AttachmentSupport = -> [Fillet008]
  ExternalBSplineMaxDegree = 0
  ExternalBSplineTolerance = 0
  ExternalGeometry = -> [Fillet008]
  FullyConstrained = false
  InternalTolerance = 1e-06
  InvalidShape = false
  MakeInternals = false
  MapMode = 5
  Placement = pos=(0,94,-3.38e-14) rot=(0,0.707107,0.707107;3.14159rad)
  Support = -> [Fillet008]
  TreeRank = 0
  ValidateShape = false
  sketch-geometry (4):
    g0: LineSegment StartX=-5.36666 StartY=-47 StartZ=0 EndX=5.36667 EndY=-47 EndZ=0
    g1: ArcOfCircle CenterX=-5.36667 CenterY=-45 CenterZ=0 NormalX=0 NormalY=0 NormalZ=1 AngleXU=0 Radius=2 StartAngle=4.71239 EndAngle=6.65039
    g2: ArcOfCircle CenterX=5.36667 CenterY=-45 CenterZ=0 NormalX=0 NormalY=0 NormalZ=1 AngleXU=0 Radius=2 StartAngle=2.77438 EndAngle=4.71239
    g3: ArcOfCircle CenterX=7e-16 CenterY=-42.9357 CenterZ=0 NormalX=0 NormalY=0 NormalZ=1 AngleXU=0 Radius=3.75 StartAngle=5.91598 EndAngle=9.79199
  constraints (11):
    c: Tangent(g0,g-3)
    c: Coincident(g1,g0)
    c: Coincident(g1,g-3)
    c: Coincident(g1,g-4)
    c: Coincident(g2,g0)
    c: Coincident(g2,g-5)
    c: Coincident(g2,g-5)
    c: Tangent(g0,g-5)
    c: Coincident(g3,g2)
    c: Coincident(g3,g1)
    c: Coincident(g3,g-4)
FEATURE [PartDesign::Pad] Pad021
  AddSubType = 0
  AutoTaperInnerAngle = true
  BaseFeature = -> Fillet008
  CheckUpToFaceLimits = true
  ClaimChildren = false
  Direction = (1,1,1)
  Fit = 0
  FitJoin = 0
  InnerFit = 0
  InnerFitJoin = 0
  InvalidShape = false
  Length = 1.5
  Length2 = 100
  NewSolid = false
  Profile = -> Sketch034
  Reversed = true
  Suppress = false
  TaperInnerAngle = 0
  TaperInnerAngleRev = 0
  TreeRank = 0
  Type = 0
  ValidateShape = true
  _ProfileBasedVersion = 0
FEATURE [PartDesign::Pocket] Pocket014
  AddSubType = 1
  AutoTaperInnerAngle = true
  BaseFeature = -> Pad021
  CheckUpToFaceLimits = true
  ClaimChildren = false
  Direction = (1,1,1)
  Fit = 0
  FitJoin = 0
  InnerFit = 0
  InnerFitJoin = 0
  InvalidShape = false
  Length = 5
  Length2 = 100
  NewSolid = false
  Profile = -> Sketch035
  Suppress = false
  TaperInnerAngle = 0
  TaperInnerAngleRev = 0
  TreeRank = 0
  Type = 1
  ValidateShape = true
  _ProfileBasedVersion = 0
  _Version = 0
FEATURE [Sketcher::SketchObject] Sketch036
  ArcFitTolerance = 0
  AttachmentSupport = -> [Pocket014]
  ExternalBSplineMaxDegree = 0
  ExternalBSplineTolerance = 0
  FullyConstrained = false
  InternalTolerance = 1e-06
  InvalidShape = false
  MakeInternals = false
  MapMode = 5
  Placement = pos=(0,0,0) rot=(0.57735,0.57735,0.57735;2.0944rad)
  Support = -> [Pocket014]
  TreeRank = 0
  ValidateShape = false
  sketch-geometry (1):
    g0: Circle CenterX=87.5 CenterY=-5 CenterZ=0 NormalX=0 NormalY=0 NormalZ=1 AngleXU=0 Radius=2
  constraints (3):
    c: Diameter(g0) = 4
    c: DistanceY(g0,g-1) = 5
    c: DistanceX(g-1,g0) = 87.5
FEATURE [PartDesign::Pad] Pad022
  AddSubType = 0
  AutoTaperInnerAngle = true
  BaseFeature = -> Pocket014
  CheckUpToFaceLimits = true
  ClaimChildren = false
  Direction = (1,1,1)
  Fit = 0
  FitJoin = 0
  InnerFit = 0
  InnerFitJoin = 0
  InvalidShape = false
  Length = 5
  Length2 = 100
  NewSolid = false
  Profile = -> Sketch036
  Suppress = false
  TaperInnerAngle = 0
  TaperInnerAngleRev = 0
  TreeRank = 0
  Type = 0
  ValidateShape = true
  _ProfileBasedVersion = 0
FEATURE [Sketcher::SketchObject] Sketch037
  ArcFitTolerance = 0
  AttachmentSupport = -> [Pad022]
  ExternalBSplineMaxDegree = 0
  ExternalBSplineTolerance = 0
  FullyConstrained = false
  InternalTolerance = 1e-06
  InvalidShape = false
  MakeInternals = false
  MapMode = 5
  Placement = pos=(0,0,0) rot=(0.57735,0.57735,0.57735;2.0944rad)
  Support = -> [Pad022]
  TreeRank = 0
  ValidateShape = false
  sketch-geometry (1):
    g0: Circle CenterX=-87.5 CenterY=-5 CenterZ=0 NormalX=0 NormalY=0 NormalZ=1 AngleXU=0 Radius=2.5
  constraints (3):
    c: Diameter(g0) = 5
    c: DistanceY(g0,g-1) = 5
    c: DistanceX(g0,g-1) = 87.5
FEATURE [PartDesign::Pocket] Pocket015
  AddSubType = 1
  AutoTaperInnerAngle = true
  BaseFeature = -> Pad022
  CheckUpToFaceLimits = true
  ClaimChildren = false
  Direction = (1,1,1)
  Fit = 0
  FitJoin = 0
  InnerFit = 0
  InnerFitJoin = 0
  InvalidShape = false
  Length = 5.5
  Length2 = 100
  NewSolid = false
  Profile = -> Sketch037
  Suppress = false
  TaperInnerAngle = 0
  TaperInnerAngleRev = 0
  TreeRank = 0
  Type = 0
  ValidateShape = true
  _ProfileBasedVersion = 0
  _Version = 0
FEATURE [PartDesign::Chamfer] Chamfer007
  AddSubType = 0
  Angle = 45
  Base = -> Pocket015 [Edge116,Edge56]
  BaseFeature = -> Pocket015
  ChamferType = 0
  FlipDirection = false
  InvalidShape = false
  NewSolid = false
  Size = 1
  Size2 = 1
  SupportTransform = true
  Suppress = false
  TreeRank = 0
  UseAllEdges = false
  ValidateShape = true
FEATURE [Sketcher::SketchObject] Sketch038
  ArcFitTolerance = 0
  AttachmentSupport = -> [Chamfer007]
  ExternalBSplineMaxDegree = 0
  ExternalBSplineTolerance = 0
  FullyConstrained = false
  InternalTolerance = 1e-06
  InvalidShape = false
  MakeInternals = false
  MapMode = 5
  Placement = pos=(0,0,0) rot=(0.57735,0.57735,0.57735;2.0944rad)
  Support = -> [Chamfer007]
  TreeRank = 0
  ValidateShape = false
  sketch-geometry (4):
    g0: Circle CenterX=87.5 CenterY=-16.69 CenterZ=0 NormalX=0 NormalY=0 NormalZ=1 AngleXU=0 Radius=1.65
    g1: Circle CenterX=87.5 CenterY=-31.69 CenterZ=0 NormalX=0 NormalY=0 NormalZ=1 AngleXU=0 Radius=1.65
    g2: Circle CenterX=-87.5 CenterY=-16.69 CenterZ=0 NormalX=0 NormalY=0 NormalZ=1 AngleXU=0 Radius=1.65
    g3: Circle CenterX=-87.5 CenterY=-31.69 CenterZ=0 NormalX=0 NormalY=0 NormalZ=1 AngleXU=0 Radius=1.65
  constraints (10):
    c: DistanceY(g0,g-1) = 16.69
    c: DistanceY(g1,g-1) = 31.69
    c: DistanceX(g-1,g0) = 87.5
    c: Symmetric(g0,g2,g-2)
    c: Symmetric(g3,g1,g-2)
    c: Vertical(g1,g0)
    c: Equal(g0,g1)
    c: Equal(g1,g2)
    c: Equal(g2,g3)
    c: Diameter(g0) = 3.3
FEATURE [PartDesign::Pocket] Pocket016
  AddSubType = 1
  AutoTaperInnerAngle = true
  BaseFeature = -> Chamfer007
  CheckUpToFaceLimits = true
  ClaimChildren = false
  Direction = (1,1,1)
  Fit = 0
  FitJoin = 0
  InnerFit = 0
  InnerFitJoin = 0
  InvalidShape = false
  Length = 5
  Length2 = 100
  NewSolid = false
  Profile = -> Sketch038
  Suppress = false
  TaperInnerAngle = 0
  TaperInnerAngleRev = 0
  TreeRank = 0
  Type = 1
  ValidateShape = true
  _ProfileBasedVersion = 0
  _Version = 0
FEATURE [Sketcher::SketchObject] Sketch039
  ArcFitTolerance = 0
  AttachmentSupport = -> [Pocket016]
  ExternalBSplineMaxDegree = 0
  ExternalBSplineTolerance = 0
  FullyConstrained = false
  InternalTolerance = 1e-06
  InvalidShape = false
  MakeInternals = false
  MapMode = 5
  Placement = pos=(-7.36667,0,-1e-16) rot=(0.57735,-0.57735,-0.57735;2.0944rad)
  Support = -> [Pocket016]
  TreeRank = 0
  ValidateShape = false
  sketch-geometry (2):
    g0: Circle CenterX=-87.5 CenterY=-31.69 CenterZ=0 NormalX=0 NormalY=0 NormalZ=1 AngleXU=0 Radius=2
    g1: Circle CenterX=-87.5 CenterY=-16.69 CenterZ=0 NormalX=0 NormalY=0 NormalZ=1 AngleXU=0 Radius=2
  constraints (6):
    c: Equal(g1,g0)
    c: Diameter(g0) = 4
    c: DistanceY(g1,g-1) = 16.69
    c: DistanceY(g0,g-1) = 31.69
    c: DistanceX(g1,g-1) = 87.5
    c: Vertical(g1,g0)
FEATURE [PartDesign::Pocket] Pocket017
  AddSubType = 1
  AutoTaperInnerAngle = true
  BaseFeature = -> Pocket016
  CheckUpToFaceLimits = true
  ClaimChildren = false
  Direction = (1,1,1)
  Fit = 0
  FitJoin = 0
  InnerFit = 0
  InnerFitJoin = 0
  InvalidShape = false
  Length = 6
  Length2 = 100
  NewSolid = false
  Profile = -> Sketch039
  Suppress = false
  TaperInnerAngle = 0
  TaperInnerAngleRev = 0
  TreeRank = 0
  Type = 0
  ValidateShape = true
  _ProfileBasedVersion = 0
  _Version = 0
FEATURE [PartDesign::Pocket] Pocket018
  AddSubType = 1
  AutoTaperInnerAngle = true
  BaseFeature = -> Pocket017
  CheckUpToFaceLimits = true
  ClaimChildren = false
  Direction = (1,1,1)
  Fit = 0
  FitJoin = 0
  InnerFit = 0
  InnerFitJoin = 0
  InvalidShape = false
  Length = 5
  Length2 = 100
  NewSolid = false
  Profile = -> Sketch039
  Reversed = true
  Suppress = false
  TaperInnerAngle = 0
  TaperInnerAngleRev = 0
  TreeRank = 0
  Type = 1
  ValidateShape = true
  _ProfileBasedVersion = 0
  _Version = 0
FEATURE [Sketcher::SketchObject] Sketch040
  ArcFitTolerance = 0
  AttachmentSupport = -> [Pocket018]
  ExternalBSplineMaxDegree = 0
  ExternalBSplineTolerance = 0
  FullyConstrained = false
  InternalTolerance = 1e-06
  InvalidShape = false
  MakeInternals = false
  MapMode = 5
  Placement = pos=(-7.36667,0,-1e-16) rot=(0.57735,-0.57735,-0.57735;2.0944rad)
  Support = -> [Pocket018]
  TreeRank = 0
  ValidateShape = false
  sketch-geometry (2):
    g0: Circle CenterX=87.5 CenterY=-16.69 CenterZ=0 NormalX=0 NormalY=0 NormalZ=1 AngleXU=0 Radius=3
    g1: Circle CenterX=87.5 CenterY=-31.69 CenterZ=0 NormalX=0 NormalY=0 NormalZ=1 AngleXU=0 Radius=3
  constraints (6):
    c: Equal(g0,g1)
    c: Diameter(g0) = 6
    c: DistanceY(g1,g-1) = 31.69
    c: DistanceY(g0,g-1) = 16.69
    c: DistanceX(g-1,g0) = 87.5
    c: Vertical(g0,g1)
FEATURE [PartDesign::Pocket] Pocket019
  AddSubType = 1
  AutoTaperInnerAngle = true
  BaseFeature = -> Pocket018
  CheckUpToFaceLimits = true
  ClaimChildren = false
  Direction = (1,1,1)
  Fit = 0
  FitJoin = 0
  InnerFit = 0
  InnerFitJoin = 0
  InvalidShape = false
  Length = 3
  Length2 = 100
  NewSolid = false
  Profile = -> Sketch040
  Suppress = false
  TaperInnerAngle = 0
  TaperInnerAngleRev = 0
  TreeRank = 0
  Type = 0
  ValidateShape = true
  _ProfileBasedVersion = 0
  _Version = 0
FEATURE [PartDesign::Pocket] Pocket020
  AddSubType = 1
  AutoTaperInnerAngle = true
  BaseFeature = -> Pocket019
  CheckUpToFaceLimits = true
  ClaimChildren = false
  Direction = (1,1,1)
  Fit = 0
  FitJoin = 0
  InnerFit = 0
  InnerFitJoin = 0
  InvalidShape = false
  Length = 5
  Length2 = 100
  NewSolid = false
  Profile = -> Sketch040
  Reversed = true
  Suppress = false
  TaperInnerAngle = 0
  TaperInnerAngleRev = 0
  TreeRank = 0
  Type = 1
  ValidateShape = true
  _ProfileBasedVersion = 0
  _Version = 0
FEATURE [PartDesign::Pocket] Pocket021
  AddSubType = 1
  AutoTaperInnerAngle = true
  BaseFeature = -> Pocket020
  CheckUpToFaceLimits = true
  ClaimChildren = false
  Direction = (1,1,1)
  Fit = 0
  FitJoin = 0
  InnerFit = 0
  InnerFitJoin = 0
  InvalidShape = false
  Length = 5
  Length2 = 100
  Midplane = true
  NewSolid = false
  Profile = -> Pocket020 [Face41]
  Suppress = false
  TaperInnerAngle = 0
  TaperInnerAngleRev = 0
  TreeRank = 0
  Type = 1
  ValidateShape = true
  _ProfileBasedVersion = 0
  _Version = 0
FEATURE [PartDesign::Body] Body004
  AutoGroupSolids = false
  ClaimAllChildren = false
  ExportMode = 0
  Group = -> [Sketch031,Pad018,Pad019,Sketch033,Pad020,Mirrored004,Fillet008,Sketch034,Pad021,Sketch035,Pocket014,Sketch036,Pad022,Sketch037,Pocket015,Chamfer007,Sketch038,Pocket016,Sketch039,Pocket017,Pocket018,Sketch040,Pocket019,Pocket020,Pocket021]
  InvalidShape = false
  Origin = -> Origin004
  SingleSolid = true
  Tip = -> Pocket021
  TreeRank = 0
  ValidateShape = false
  _ExportChildren = -> [Pad018,Pad019,Pad020,Mirrored004,Fillet008,Pad021,Pocket014,Pad022,Pocket015,Chamfer007,Pocket016,Pocket017,Pocket018,Pocket019,Pocket020,Pocket021]
  _GroupVersion = 1
COMPONENT P5 — recipe-attached ("Body005", modeled in this document).
Construction recipe (the document's own serialized feature program — sketch geometry with constraints, then the solid features built on it; lengths are millimeters unless a unit is written):

FEATURE [Sketcher::SketchObject] Sketch043
  ArcFitTolerance = 0
  AttachmentSupport = -> [XY_Plane005]
  ExternalBSplineMaxDegree = 0
  ExternalBSplineTolerance = 0
  FullyConstrained = false
  InternalTolerance = 1e-06
  InvalidShape = false
  MakeInternals = false
  MapMode = 5
  Support = -> [XY_Plane005]
  TreeRank = 0
  ValidateShape = false
  sketch-geometry (10):
    g0: LineSegment [constr] StartX=0 StartY=0 StartZ=0 EndX=2 EndY=0 EndZ=0
    g1: LineSegment StartX=2 StartY=0 StartZ=0 EndX=2 EndY=6 EndZ=0
    g2: LineSegment StartX=2 StartY=6 StartZ=0 EndX=0 EndY=6 EndZ=0
    g3: LineSegment StartX=0 StartY=6 StartZ=0 EndX=0 EndY=78 EndZ=0
    g4: LineSegment StartX=0 StartY=78 StartZ=0 EndX=3 EndY=78 EndZ=0
    g5: LineSegment StartX=3 StartY=78 StartZ=0 EndX=3 EndY=27.5 EndZ=0
    g6: LineSegment StartX=3 StartY=27.5 StartZ=0 EndX=12.5 EndY=20 EndZ=0
    g7: LineSegment StartX=12.5 StartY=20 StartZ=0 EndX=12.5 EndY=0 EndZ=0
    g8: LineSegment StartX=12.5 StartY=0 StartZ=0 EndX=2 EndY=0 EndZ=0
    g9: GeomPoint [constr] X=-12.5 Y=0 Z=0
  constraints (27):
    c: Coincident(g0,g-1)
    c: PointOnObject(g0,g-1)
    c: Coincident(g1,g0)
    c: Vertical(g1)
    c: Coincident(g1,g2)
    c: PointOnObject(g2,g-2)
    c: Horizontal(g2)
    c: Coincident(g2,g3)
    c: PointOnObject(g3,g-2)
    c: Coincident(g4,g3)
    c: Horizontal(g4)
    c: Coincident(g4,g5)
    c: Vertical(g5)
    c: Coincident(g5,g6)
    c: Coincident(g6,g7)
    c: PointOnObject(g7,g-1)
    c: Vertical(g7)
    c: Coincident(g7,g8)
    c: Coincident(g8,g0)
    c: DistanceY(g1,g1) = 6
    c: DistanceX(g2,g2) = 2
    c: DistanceX(g4,g4) = 3
    c: DistanceY(g-1,g3) = 78
    c: DistanceY(g7,g7) = 20
    c: DistanceY(g6,g5) = 7.5
    c: Symmetric(g9,g7,g-2)
    c: DistanceX(g9,g7) = 25
FEATURE [PartDesign::Revolution] Revolution
  AddSubType = 0
  Angle = 360
  Axis = (0,1,0)
  Base = (0,0,0)
  ClaimChildren = false
  Fit = 0
  FitJoin = 0
  InnerFit = 0
  InnerFitJoin = 0
  InvalidShape = false
  NewSolid = false
  Profile = -> Sketch043
  ReferenceAxis = -> Sketch043 [V_Axis]
  Reversed = true
  Suppress = false
  TreeRank = 0
  ValidateShape = true
  _ProfileBasedVersion = 0
FEATURE [Sketcher::SketchObject] Sketch041
  ArcFitTolerance = 0
  AttachmentSupport = -> [Revolution]
  ExternalBSplineMaxDegree = 0
  ExternalBSplineTolerance = 0
  ExternalGeometry = -> [Revolution]
  FullyConstrained = false
  InternalTolerance = 1e-06
  InvalidShape = false
  MakeInternals = false
  MapMode = 5
  Placement = pos=(0,0,0) rot=(1,0,0;1.5708rad)
  Support = -> [Revolution]
  TreeRank = 0
  ValidateShape = false
  sketch-geometry (1):
    g0: Circle CenterX=0 CenterY=12.5 CenterZ=0 NormalX=0 NormalY=0 NormalZ=1 AngleXU=0 Radius=1.5
  constraints (3):
    c: PointOnObject(g0,g-2)
    c: PointOnObject(g0,g-3)
    c: Diameter(g0) = 3
FEATURE [PartDesign::Pocket] Pocket022
  AddSubType = 1
  AutoTaperInnerAngle = true
  BaseFeature = -> Revolution
  CheckUpToFaceLimits = true
  ClaimChildren = false
  Direction = (1,1,1)
  Fit = 0
  FitJoin = 0
  InnerFit = 0
  InnerFitJoin = 0
  InvalidShape = false
  Length = 5
  Length2 = 100
  NewSolid = false
  Profile = -> Sketch041
  Suppress = false
  TaperInnerAngle = 0
  TaperInnerAngleRev = 0
  TreeRank = 0
  Type = 1
  ValidateShape = true
  _ProfileBasedVersion = 0
  _Version = 0
FEATURE [PartDesign::PolarPattern] PolarPattern
  AddSubType = 0
  Angle = 360
  Axis = -> Sketch041 [N_Axis]
  BaseFeature = -> Pocket022
  CopyShape = true
  InvalidShape = false
  NewSolid = false
  Occurrences = 8
  OriginalSubs = -> [Pocket022]
  Originals = -> [Pocket022]
  ParallelTransform = true
  SubTransform = true
  Suppress = false
  TreeRank = 0
  ValidateShape = true
  _Version = 0
FEATURE [PartDesign::Fillet] Fillet009
  AddSubType = 0
  Base = -> PolarPattern [Face15,Face13,Face11,Face9,Face7,Face5,Face19,Face17]
  BaseFeature = -> PolarPattern
  InvalidShape = false
  NewSolid = false
  Radius = 1.25
  SupportTransform = true
  Suppress = false
  TreeRank = 0
  UseAllEdges = false
  ValidateShape = true
FEATURE [PartDesign::Fillet] Fillet010
  AddSubType = 0
  Base = -> Fillet009 [Edge94]
  BaseFeature = -> Fillet009
  InvalidShape = false
  NewSolid = false
  Radius = 10
  SupportTransform = true
  Suppress = false
  TreeRank = 0
  UseAllEdges = false
  ValidateShape = true
FEATURE [PartDesign::Chamfer] Chamfer008
  AddSubType = 0
  Angle = 45
  Base = -> Fillet010 [Edge144]
  BaseFeature = -> Fillet010
  ChamferType = 0
  FlipDirection = false
  InvalidShape = false
  NewSolid = false
  Size = 0.5
  Size2 = 1
  SupportTransform = true
  Suppress = false
  TreeRank = 0
  UseAllEdges = false
  ValidateShape = true
FEATURE [Sketcher::SketchObject] Sketch042
  ArcFitTolerance = 0
  AttachmentSupport = -> [Chamfer008]
  ExternalBSplineMaxDegree = 0
  ExternalBSplineTolerance = 0
  FullyConstrained = false
  InternalTolerance = 1e-06
  InvalidShape = false
  MakeInternals = false
  MapMode = 5
  Placement = pos=(0,6,0) rot=(1,0,0;1.5708rad)
  Support = -> [Chamfer008]
  TreeRank = 0
  ValidateShape = false
  sketch-geometry (1):
    g0: Circle CenterX=0 CenterY=0 CenterZ=0 NormalX=0 NormalY=0 NormalZ=1 AngleXU=0 Radius=1.5
  constraints (2):
    c: Coincident(g0,g-1)
    c: Diameter(g0) = 3
FEATURE [PartDesign::Pocket] Pocket023
  AddSubType = 1
  AutoTaperInnerAngle = true
  BaseFeature = -> Chamfer008
  CheckUpToFaceLimits = true
  ClaimChildren = false
  Direction = (1,1,1)
  Fit = 0
  FitJoin = 0
  InnerFit = 0
  InnerFitJoin = 0
  InvalidShape = false
  Length = 12
  Length2 = 100
  NewSolid = false
  Profile = -> Sketch042
  Suppress = false
  TaperInnerAngle = 0
  TaperInnerAngleRev = 0
  TreeRank = 0
  Type = 0
  ValidateShape = true
  _ProfileBasedVersion = 0
  _Version = 0
FEATURE [PartDesign::Chamfer] Chamfer009
  AddSubType = 0
  Angle = 45
  Base = -> Pocket023 [Edge153]
  BaseFeature = -> Pocket023
  ChamferType = 0
  FlipDirection = false
  InvalidShape = false
  NewSolid = false
  Size = 0.25
  Size2 = 1
  SupportTransform = true
  Suppress = false
  TreeRank = 0
  UseAllEdges = false
  ValidateShape = true
FEATURE [Part::Part2DObjectPython] InvoluteGear003  # Draft 2D object (typed FeaturePython)
  AddendumCoefficient = 1
  AttachmentSupport = -> [Chamfer009]
  DedendumCoefficient = 1.25
  ExternalGear = true
  HighPrecision = true
  InvalidShape = false
  MapMode = 5
  Modules = 1.3
  NumberOfTeeth = 26
  Placement = pos=(0,78,0) rot=(0,0.707107,0.707107;3.14159rad)
  PressureAngle = 20
  ProfileShiftCoefficient = 0
  RootFilletCoefficient = 0.375
  Support = -> [Chamfer009]
  TreeRank = 0
  ValidateShape = false
FEATURE [PartDesign::Pad] Pad036
  AddSubType = 0
  AutoTaperInnerAngle = true
  BaseFeature = -> Chamfer009
  CheckUpToFaceLimits = true
  ClaimChildren = false
  Direction = (1,1,1)
  Fit = 0
  FitJoin = 0
  InnerFit = 0
  InnerFitJoin = 0
  InvalidShape = false
  Length = 9
  Length2 = 100
  NewSolid = false
  Profile = -> InvoluteGear003
  Suppress = false
  TaperInnerAngle = 0
  TaperInnerAngleRev = 0
  TreeRank = 0
  Type = 0
  ValidateShape = true
  _ProfileBasedVersion = 0
FEATURE [Sketcher::SketchObject] Sketch079
  ArcFitTolerance = 0
  AttachmentSupport = -> [Pad036]
  ExternalBSplineMaxDegree = 0
  ExternalBSplineTolerance = 0
  FullyConstrained = false
  InternalTolerance = 1e-06
  InvalidShape = false
  MakeInternals = false
  MapMode = 5
  Placement = pos=(0,78,0) rot=(1,0,0;1.5708rad)
  Support = -> [Pad036]
  TreeRank = 0
  ValidateShape = false
  sketch-geometry (2):
    g0: Circle CenterX=0 CenterY=0 CenterZ=0 NormalX=0 NormalY=0 NormalZ=1 AngleXU=0 Radius=7.5
    g1: Circle CenterX=0 CenterY=0 CenterZ=0 NormalX=0 NormalY=0 NormalZ=1 AngleXU=0 Radius=3
  constraints (4):
    c: Coincident(g0,g-1)
    c: Diameter(g0) = 15
    c: Coincident(g1,g0)
    c: Diameter(g1) = 6
FEATURE [PartDesign::Pad] Pad037
  AddSubType = 0
  AutoTaperInnerAngle = true
  BaseFeature = -> Pad036
  CheckUpToFaceLimits = true
  ClaimChildren = false
  Direction = (1,1,1)
  Fit = 0
  FitJoin = 0
  InnerFit = 0
  InnerFitJoin = 0
  InvalidShape = false
  Length = 4.5
  Length2 = 100
  NewSolid = false
  Profile = -> Sketch079
  Suppress = false
  TaperInnerAngle = 0
  TaperInnerAngleRev = 0
  TreeRank = 0
  Type = 0
  ValidateShape = true
  _ProfileBasedVersion = 0
FEATURE [PartDesign::SubShapeBinder] Binder001
  BindCopyOnChange = 0
  BindMode = 0
  ClaimChildren = false
  Context = -> Assembly002 [Parts002.Assembly006.Parts006.Body005.Binder001.]
  EdgeTolerance = 1e-06
  FillStyle = 0
  Fuse = false
  InvalidShape = false
  MakeFace = true
  MergeEdges = true
  OffsetFill = false
  OffsetIntersection = false
  OffsetJoinType = 0
  OffsetOpenResult = false
  Outline = false
  PartialLoad = false
  Refine = true
  Relative = true
  SplitEdges = false
  Support = -> [Plane010]
  TightBound = false
  TreeRank = 0
  ValidateShape = false
  _Version = 3
FEATURE [Sketcher::SketchObject] Sketch080
  ArcFitTolerance = 0
  AttachmentSupport = -> [Binder001]
  ExternalBSplineMaxDegree = 0
  ExternalBSplineTolerance = 0
  FullyConstrained = false
  InternalTolerance = 1e-06
  InvalidShape = false
  MakeInternals = false
  MapMode = 5
  Placement = pos=(0,58.5,0) rot=(0,0.707107,0.707107;3.14159rad)
  Support = -> [Binder001]
  TreeRank = 0
  ValidateShape = false
  sketch-geometry (2):
    g0: Circle CenterX=0 CenterY=0 CenterZ=0 NormalX=0 NormalY=0 NormalZ=1 AngleXU=0 Radius=3
    g1: Circle CenterX=0 CenterY=0 CenterZ=0 NormalX=0 NormalY=0 NormalZ=1 AngleXU=0 Radius=7.5
  constraints (4):
    c: Coincident(g0,g-1)
    c: Coincident(g1,g0)
    c: Diameter(g0) = 6
    c: Diameter(g1) = 15
FEATURE [PartDesign::Pad] Pad038
  AddSubType = 0
  AutoTaperInnerAngle = true
  BaseFeature = -> Pad037
  CheckUpToFaceLimits = true
  ClaimChildren = false
  Direction = (1,1,1)
  Fit = 0
  FitJoin = 0
  InnerFit = 0
  InnerFitJoin = 0
  InvalidShape = false
  Length = 5
  Length2 = 100
  NewSolid = false
  Profile = -> Sketch080
  Reversed = true
  Suppress = false
  TaperInnerAngle = 0
  TaperInnerAngleRev = 0
  TreeRank = 0
  Type = 0
  ValidateShape = true
  _ProfileBasedVersion = 0
FEATURE [PartDesign::Fillet] Fillet020
  AddSubType = 0
  Base = -> Pad038 [Face326]
  BaseFeature = -> Pad038
  InvalidShape = false
  NewSolid = false
  Radius = 0.7
  SupportTransform = true
  Suppress = false
  TreeRank = 0
  UseAllEdges = false
  ValidateShape = true
FEATURE [PartDesign::Fillet] Fillet021
  AddSubType = 0
  Base = -> Fillet020 [Edge269]
  BaseFeature = -> Fillet020
  InvalidShape = false
  NewSolid = false
  Radius = 3
  SupportTransform = true
  Suppress = false
  TreeRank = 0
  UseAllEdges = false
  ValidateShape = true
FEATURE [PartDesign::Chamfer] Chamfer029
  AddSubType = 0
  Angle = 45
  Base = -> Fillet021 [Edge785,Edge1310,Edge1312]
  BaseFeature = -> Fillet021
  ChamferType = 0
  FlipDirection = false
  InvalidShape = false
  NewSolid = false
  Size = 1
  Size2 = 1
  SupportTransform = true
  Suppress = false
  TreeRank = 0
  UseAllEdges = false
  ValidateShape = true
FEATURE [PartDesign::Body] Body005
  AutoGroupSolids = false
  ClaimAllChildren = false
  ExportMode = 0
  Group = -> [Sketch043,Revolution,Sketch041,Pocket022,PolarPattern,Fillet009,Fillet010,Chamfer008,Sketch042,Pocket023,Chamfer009,InvoluteGear003,Pad036,Sketch079,Pad037,Binder001,Sketch080,Pad038,Fillet020,Fillet021,Chamfer029]
  InvalidShape = false
  Origin = -> Origin005
  SingleSolid = true
  Tip = -> Chamfer029
  TreeRank = 0
  ValidateShape = false
  _ExportChildren = -> [Revolution,Pocket022,PolarPattern,Fillet009,Fillet010,Chamfer008,Pocket023,Chamfer009,Pad036,Pad037,Binder001,Pad038,Fillet020,Fillet021,Chamfer029]
  _GroupVersion = 1
COMPONENT P6 — recipe-attached ("Body006", modeled in this document).
Construction recipe (the document's own serialized feature program — sketch geometry with constraints, then the solid features built on it; lengths are millimeters unless a unit is written):

FEATURE [Sketcher::SketchObject] Sketch044
  ArcFitTolerance = 0
  AttachmentSupport = -> [XY_Plane006]
  ExternalBSplineMaxDegree = 0
  ExternalBSplineTolerance = 0
  FullyConstrained = false
  InternalTolerance = 1e-06
  InvalidShape = false
  MakeInternals = false
  MapMode = 5
  Support = -> [XY_Plane006]
  TreeRank = 0
  ValidateShape = false
  sketch-geometry (2):
    g0: Circle CenterX=0 CenterY=0 CenterZ=0 NormalX=0 NormalY=0 NormalZ=1 AngleXU=0 Radius=150
    g1: Circle CenterX=0 CenterY=0 CenterZ=0 NormalX=0 NormalY=0 NormalZ=1 AngleXU=0 Radius=3.5
  constraints (4):
    c: Coincident(g0,g-1)
    c: Radius(g0) = 150
    c: Coincident(g1,g0)
    c: Diameter(g1) = 7
FEATURE [PartDesign::Pad] Pad023
  AddSubType = 0
  AllowMultiFace = false
  AutoTaperInnerAngle = true
  CheckUpToFaceLimits = true
  ClaimChildren = false
  Direction = (1,1,1)
  Fit = 0
  FitJoin = 0
  InnerFit = 0
  InnerFitJoin = 0
  InvalidShape = false
  Length = 3.5
  Length2 = 100
  Midplane = true
  NewSolid = false
  Profile = -> Sketch044
  Suppress = false
  TaperInnerAngle = 0
  TaperInnerAngleRev = 0
  TreeRank = 0
  Type = 0
  ValidateShape = true
  _ProfileBasedVersion = 0
FEATURE [PartDesign::Fillet] Fillet011
  AddSubType = 0
  Base = -> Pad023 [Face1]
  BaseFeature = -> Pad023
  InvalidShape = false
  NewSolid = false
  Radius = 0.5
  SupportTransform = false
  Suppress = false
  TreeRank = 0
  UseAllEdges = false
  ValidateShape = true
FEATURE [Sketcher::SketchObject] Sketch045
  ArcFitTolerance = 0
  ExternalBSplineMaxDegree = 0
  ExternalBSplineTolerance = 0
  FullyConstrained = false
  InternalTolerance = 1e-06
  InvalidShape = false
  MakeInternals = false
  MapMode = 5
  Placement = pos=(0,0,1.75) rot=(0,0,1;0rad)
  TreeRank = 0
  ValidateShape = false
  sketch-geometry (2):
    g0: Circle CenterX=0 CenterY=0 CenterZ=0 NormalX=0 NormalY=0 NormalZ=1 AngleXU=0 Radius=50
    g1: Circle CenterX=0 CenterY=0 CenterZ=0 NormalX=0 NormalY=0 NormalZ=1 AngleXU=0 Radius=60
  constraints (4):
    c: Coincident(g0,g-1)
    c: Coincident(g1,g0)
    c: Diameter(g0) = 100
    c: Diameter(g1) = 120
FEATURE [PartDesign::Pocket] Pocket024
  AddSubType = 1
  AllowMultiFace = false
  AutoTaperInnerAngle = true
  BaseFeature = -> Fillet011
  CheckUpToFaceLimits = true
  ClaimChildren = false
  Direction = (1,1,1)
  Fit = 0
  FitJoin = 0
  InnerFit = 0
  InnerFitJoin = 0
  InvalidShape = false
  Length = 0.5
  Length2 = 100
  NewSolid = false
  Profile = -> Sketch045
  Suppress = false
  TaperInnerAngle = 0
  TaperInnerAngleRev = 0
  TreeRank = 0
  Type = 0
  ValidateShape = true
  _ProfileBasedVersion = 0
  _Version = 0
FEATURE [PartDesign::Mirrored] Mirrored006
  AddSubType = 0
  BaseFeature = -> Pocket024
  CopyShape = true
  InvalidShape = false
  MirrorPlane = -> XY_Plane006
  NewSolid = false
  OriginalSubs = -> [Pocket024]
  Originals = -> [Pocket024]
  ParallelTransform = true
  SubTransform = true
  Suppress = false
  TreeRank = 0
  ValidateShape = true
  _Version = 0
FEATURE [PartDesign::Body] Body006
  AutoGroupSolids = false
  ClaimAllChildren = false
  ExportMode = 0
  Group = -> [Sketch044,Pad023,Fillet011,Sketch045,Pocket024,Mirrored006]
  InvalidShape = false
  Origin = -> Origin006
  SingleSolid = true
  Tip = -> Mirrored006
  TreeRank = 0
  ValidateShape = false
  _ExportChildren = -> [Pad023,Fillet011,Pocket024,Mirrored006]
  _GroupVersion = 1
COMPONENT P7 — recipe-attached ("Body007", modeled in this document).
Construction recipe (the document's own serialized feature program — sketch geometry with constraints, then the solid features built on it; lengths are millimeters unless a unit is written):

FEATURE [PartDesign::ShapeBinder] CopyMirrored002
  InvalidShape = false
  TraceSupport = false
  TreeRank = 0
  ValidateShape = false
FEATURE [Sketcher::SketchObject] Sketch046
  ArcFitTolerance = 0
  AttachmentSupport = -> [CopyMirrored002]
  ExternalBSplineMaxDegree = 0
  ExternalBSplineTolerance = 0
  FullyConstrained = false
  InternalTolerance = 1e-06
  InvalidShape = false
  MakeInternals = false
  MapMode = 5
  Placement = pos=(0,0,1.75) rot=(0,0,1;0rad)
  Support = -> [CopyMirrored002]
  TreeRank = 0
  ValidateShape = false
  sketch-geometry (2):
    g0: Circle CenterX=0 CenterY=0 CenterZ=0 NormalX=0 NormalY=0 NormalZ=1 AngleXU=0 Radius=62
    g1: Circle [constr] CenterX=0 CenterY=0 CenterZ=0 NormalX=0 NormalY=0 NormalZ=1 AngleXU=0 Radius=52
  constraints (4):
    c: Coincident(g0,g-1)
    c: Radius(g0) = 62
    c: Coincident(g1,g0)
    c: Radius(g1) = 52
FEATURE [PartDesign::Pad] Pad024
  AddSubType = 0
  AllowMultiFace = false
  AutoTaperInnerAngle = true
  CheckUpToFaceLimits = true
  ClaimChildren = false
  Direction = (1,1,1)
  Fit = 0
  FitJoin = 0
  InnerFit = 0
  InnerFitJoin = 0
  InvalidShape = false
  Length = 6
  Length2 = 100
  NewSolid = false
  Profile = -> Sketch046
  Suppress = false
  TaperInnerAngle = 0
  TaperInnerAngleRev = 0
  TreeRank = 0
  Type = 0
  ValidateShape = true
  _ProfileBasedVersion = 0
FEATURE [Sketcher::SketchObject] Sketch047
  ArcFitTolerance = 0
  ExternalBSplineMaxDegree = 0
  ExternalBSplineTolerance = 0
  FullyConstrained = false
  InternalTolerance = 1e-06
  InvalidShape = false
  MakeInternals = false
  MapMode = 5
  Placement = pos=(0,0,-8.25) rot=(1,0,0;3.14159rad)
  TreeRank = 0
  ValidateShape = false
  sketch-geometry (1):
    g0: Circle CenterX=0 CenterY=0 CenterZ=0 NormalX=0 NormalY=0 NormalZ=1 AngleXU=0 Radius=4
  constraints (2):
    c: Coincident(g0,g-1)
    c: Diameter(g0) = 8
FEATURE [PartDesign::Pocket] Pocket026
  AddSubType = 1
  AllowMultiFace = false
  AutoTaperInnerAngle = true
  BaseFeature = -> Pad024
  CheckUpToFaceLimits = true
  ClaimChildren = false
  Direction = (1,1,1)
  Fit = 0
  FitJoin = 0
  InnerFit = 0
  InnerFitJoin = 0
  InvalidShape = false
  Length = 5
  Length2 = 100
  Midplane = true
  NewSolid = false
  Profile = -> Sketch047
  Reversed = true
  Suppress = false
  TaperInnerAngle = 0
  TaperInnerAngleRev = 0
  TreeRank = 0
  Type = 1
  ValidateShape = true
  _ProfileBasedVersion = 0
  _Version = 0
FEATURE [Sketcher::SketchObject] Sketch048
  ArcFitTolerance = 0
  ExternalBSplineMaxDegree = 0
  ExternalBSplineTolerance = 0
  FullyConstrained = false
  InternalTolerance = 1e-06
  InvalidShape = false
  MakeInternals = false
  MapMode = 5
  Placement = pos=(0,0,1.75) rot=(1,0,0;3.14159rad)
  TreeRank = 0
  ValidateShape = false
  sketch-geometry (2):
    g0: Circle CenterX=0 CenterY=0 CenterZ=0 NormalX=0 NormalY=0 NormalZ=1 AngleXU=0 Radius=53.5
    g1: Circle CenterX=0 CenterY=0 CenterZ=0 NormalX=0 NormalY=0 NormalZ=1 AngleXU=0 Radius=56.5
  constraints (4):
    c: Coincident(g0,g-1)
    c: Coincident(g1,g0)
    c: Diameter(g0) = 107
    c: Diameter(g1) = 113
FEATURE [PartDesign::Pocket] Pocket027
  AddSubType = 1
  AllowMultiFace = false
  AutoTaperInnerAngle = true
  BaseFeature = -> Pocket026
  CheckUpToFaceLimits = true
  ClaimChildren = false
  Direction = (1,1,1)
  Fit = 0
  FitJoin = 0
  InnerFit = 0
  InnerFitJoin = 0
  InvalidShape = false
  Length = 3
  Length2 = 100
  NewSolid = false
  Profile = -> Sketch048
  Suppress = false
  TaperInnerAngle = 0
  TaperInnerAngleRev = 0
  TreeRank = 0
  Type = 0
  ValidateShape = true
  _ProfileBasedVersion = 0
  _Version = 0
FEATURE [PartDesign::Draft] Draft003
  AddSubType = 0
  Angle = 5
  Base = -> Pocket027 [Face8]
  BaseFeature = -> Pocket027
  InvalidShape = false
  NeutralPlane = -> Pocket027 [Face3]
  NewSolid = false
  SupportTransform = false
  Suppress = false
  TreeRank = 0
  ValidateShape = true
FEATURE [PartDesign::Draft] Draft004
  AddSubType = 0
  Angle = 5
  Base = -> Draft003 [Face8]
  BaseFeature = -> Draft003
  InvalidShape = false
  NeutralPlane = -> Draft003 [Face7]
  NewSolid = false
  SupportTransform = false
  Suppress = false
  TreeRank = 0
  ValidateShape = true
FEATURE [PartDesign::Chamfer] Chamfer012
  AddSubType = 0
  Angle = 45
  Base = -> Draft004 [Face1]
  BaseFeature = -> Draft004
  ChamferType = 0
  FlipDirection = false
  InvalidShape = false
  NewSolid = false
  Size = 1
  Size2 = 1
  SupportTransform = true
  Suppress = false
  TreeRank = 0
  UseAllEdges = false
  ValidateShape = true
FEATURE [Sketcher::SketchObject] Sketch049
  ArcFitTolerance = 0
  AttachmentSupport = -> [YZ_Plane007]
  ExternalBSplineMaxDegree = 0
  ExternalBSplineTolerance = 0
  ExternalGeometry = -> [Chamfer012]
  FullyConstrained = false
  InternalTolerance = 1e-06
  InvalidShape = false
  MakeInternals = false
  MapMode = 5
  Placement = pos=(0,0,0) rot=(0.57735,0.57735,0.57735;2.0944rad)
  Support = -> [YZ_Plane007]
  TreeRank = 0
  ValidateShape = false
  sketch-geometry (9):
    g0: LineSegment StartX=4 StartY=7.75 StartZ=0 EndX=4 EndY=12.75 EndZ=0
    g1: LineSegment StartX=4 StartY=12.75 StartZ=0 EndX=5 EndY=12.75 EndZ=0
    g2: LineSegment StartX=5 StartY=12.75 StartZ=0 EndX=5 EndY=14.75 EndZ=0
    g3: LineSegment StartX=5 StartY=14.75 StartZ=0 EndX=4 EndY=14.75 EndZ=0
    g4: LineSegment StartX=4 StartY=14.75 StartZ=0 EndX=4 EndY=17.75 EndZ=0
    g5: LineSegment StartX=4 StartY=17.75 StartZ=0 EndX=12.5 EndY=17.75 EndZ=0
    g6: LineSegment StartX=12.5 StartY=17.75 StartZ=0 EndX=12.5 EndY=7.75 EndZ=0
    g7: LineSegment StartX=12.5 StartY=7.75 StartZ=0 EndX=4 EndY=7.75 EndZ=0
    g8: GeomPoint [constr] X=-12.5 Y=7.75 Z=0
  constraints (24):
    c: Vertical(g0)
    c: Coincident(g0,g1)
    c: Horizontal(g1)
    c: Coincident(g1,g2)
    c: Vertical(g2)
    c: Coincident(g2,g3)
    c: Horizontal(g3)
    c: Coincident(g3,g4)
    c: Vertical(g4)
    c: Coincident(g4,g5)
    c: Horizontal(g5)
    c: Coincident(g5,g6)
    c: Vertical(g6)
    c: Coincident(g6,g7)
    c: Coincident(g7,g0)
    c: Horizontal(g7)
    c: DistanceY(g6,g6) = 10
    c: Symmetric(g6,g8,g-2)
    c: DistanceX(g8,g6) = 25
    c: DistanceY(g0,g0) = 5
    c: DistanceY(g2,g2) = 2
    c: DistanceX(g1,g1) = 1
    c: Vertical(g3,g0)
    c: Coincident(g0,g-3)
FEATURE [PartDesign::Revolution] Revolution001
  AddSubType = 0
  Angle = 360
  Axis = (-2e-16,3e-16,1)
  Base = (0,0,0)
  BaseFeature = -> Chamfer012
  ClaimChildren = false
  Fit = 0
  FitJoin = 0
  InnerFit = 0
  InnerFitJoin = 0
  InvalidShape = false
  NewSolid = false
  Profile = -> Sketch049
  ReferenceAxis = -> Sketch049 [V_Axis]
  Reversed = true
  Suppress = false
  TreeRank = 0
  ValidateShape = true
  _ProfileBasedVersion = 0
FEATURE [PartDesign::Fillet] Fillet012
  AddSubType = 0
  Base = -> Revolution001 [Edge9]
  BaseFeature = -> Revolution001
  InvalidShape = false
  NewSolid = false
  Radius = 4
  SupportTransform = true
  Suppress = false
  TreeRank = 0
  UseAllEdges = false
  ValidateShape = true
FEATURE [Sketcher::SketchObject] Sketch050
  ArcFitTolerance = 0
  AttachmentSupport = -> [XZ_Plane007]
  ExternalBSplineMaxDegree = 0
  ExternalBSplineTolerance = 0
  FullyConstrained = false
  InternalTolerance = 1e-06
  InvalidShape = false
  MakeInternals = false
  MapMode = 5
  Placement = pos=(0,0,0) rot=(1,0,0;1.5708rad)
  Support = -> [XZ_Plane007]
  TreeRank = 0
  ValidateShape = false
  sketch-geometry (2):
    g0: Circle CenterX=14.5 CenterY=13 CenterZ=0 NormalX=0 NormalY=0 NormalZ=1 AngleXU=0 Radius=4.5
    g1: Circle CenterX=-14.5 CenterY=13 CenterZ=0 NormalX=0 NormalY=0 NormalZ=1 AngleXU=0 Radius=4.5
  constraints (5):
    c: Equal(g1,g0)
    c: Symmetric(g1,g0,g-2)
    c: DistanceY(g-1,g0) = 13
    c: DistanceX(g-1,g0) = 14.5
    c: Diameter(g0) = 9
FEATURE [PartDesign::Pocket] Pocket025
  AddSubType = 1
  AutoTaperInnerAngle = true
  BaseFeature = -> Fillet012
  CheckUpToFaceLimits = true
  ClaimChildren = false
  Direction = (1,1,1)
  Fit = 0
  FitJoin = 0
  InnerFit = 0
  InnerFitJoin = 0
  InvalidShape = false
  Length = 5
  Length2 = 100
  Midplane = true
  NewSolid = false
  Profile = -> Sketch050
  Suppress = false
  TaperInnerAngle = 0
  TaperInnerAngleRev = 0
  TreeRank = 0
  Type = 1
  ValidateShape = true
  _ProfileBasedVersion = 0
  _Version = 0
FEATURE [PartDesign::Chamfer] Chamfer010
  AddSubType = 0
  Angle = 45
  Base = -> Pocket025 [Face9]
  BaseFeature = -> Pocket025
  ChamferType = 0
  FlipDirection = false
  InvalidShape = false
  NewSolid = false
  Size = 0.5
  Size2 = 1
  SupportTransform = true
  Suppress = false
  TreeRank = 0
  UseAllEdges = false
  ValidateShape = true
FEATURE [PartDesign::Chamfer] Chamfer011
  AddSubType = 0
  Angle = 45
  Base = -> Chamfer010 [Face23,Edge32]
  BaseFeature = -> Chamfer010
  ChamferType = 0
  FlipDirection = false
  InvalidShape = false
  NewSolid = false
  Size = 0.5
  Size2 = 1
  SupportTransform = true
  Suppress = false
  TreeRank = 0
  UseAllEdges = false
  ValidateShape = true
FEATURE [PartDesign::Body] Body007
  AutoGroupSolids = false
  ClaimAllChildren = false
  ExportMode = 0
  Group = -> [CopyMirrored002,Sketch046,Pad024,Sketch047,Pocket026,Sketch048,Pocket027,Draft003,Draft004,Chamfer012,Sketch049,Revolution001,Fillet012,Sketch050,Pocket025,Chamfer010,Chamfer011]
  InvalidShape = false
  Origin = -> Origin007
  SingleSolid = true
  Tip = -> Chamfer011
  TreeRank = 0
  ValidateShape = false
  _ExportChildren = -> [CopyMirrored002,Pad024,Pocket026,Pocket027,Draft003,Draft004,Chamfer012,Revolution001,Fillet012,Pocket025,Chamfer010,Chamfer011]
  _GroupVersion = 1
COMPONENT P8 — recipe-attached ("Body008", modeled in this document).
Construction recipe (the document's own serialized feature program — sketch geometry with constraints, then the solid features built on it; lengths are millimeters unless a unit is written):

FEATURE [Sketcher::SketchObject] Sketch051
  ArcFitTolerance = 0
  AttachmentSupport = -> [XY_Plane008]
  ExternalBSplineMaxDegree = 0
  ExternalBSplineTolerance = 0
  FullyConstrained = false
  InternalTolerance = 1e-06
  InvalidShape = false
  MakeInternals = false
  MapMode = 5
  Support = -> [XY_Plane008]
  TreeRank = 0
  ValidateShape = false
  sketch-geometry (4):
    g0: Circle [constr] CenterX=0 CenterY=0 CenterZ=0 NormalX=0 NormalY=0 NormalZ=1 AngleXU=0 Radius=3
    g1: Circle [constr] CenterX=0 CenterY=0 CenterZ=0 NormalX=0 NormalY=0 NormalZ=1 AngleXU=0 Radius=4
    g2: Circle CenterX=0 CenterY=0 CenterZ=0 NormalX=0 NormalY=0 NormalZ=1 AngleXU=0 Radius=3.125
    g3: Circle CenterX=0 CenterY=0 CenterZ=0 NormalX=0 NormalY=0 NormalZ=1 AngleXU=0 Radius=3.875
  constraints (8):
    c: Coincident(g0,g-1)
    c: Coincident(g1,g0)
    c: Diameter(g0) = 6
    c: Diameter(g1) = 8
    c: Coincident(g2,g-1)
    c: Coincident(g3,g2)
    c: Diameter(g2) = 6.25
    c: Diameter(g3) = 7.75
FEATURE [PartDesign::Pad] Pad025
  AddSubType = 0
  AutoTaperInnerAngle = true
  CheckUpToFaceLimits = true
  ClaimChildren = false
  Direction = (1,1,1)
  Fit = 0
  FitJoin = 0
  InnerFit = 0
  InnerFitJoin = 0
  InvalidShape = false
  Length = 16
  Length2 = 100
  NewSolid = false
  Profile = -> Sketch051
  Suppress = false
  TaperInnerAngle = 0
  TaperInnerAngleRev = 0
  TreeRank = 0
  Type = 0
  ValidateShape = true
  _ProfileBasedVersion = 0
FEATURE [Sketcher::SketchObject] Sketch052
  ArcFitTolerance = 0
  AttachmentSupport = -> [Pad025]
  ExternalBSplineMaxDegree = 0
  ExternalBSplineTolerance = 0
  ExternalGeometry = -> [Pad025]
  FullyConstrained = false
  InternalTolerance = 1e-06
  InvalidShape = false
  MakeInternals = false
  MapMode = 5
  Placement = pos=(0,0,16) rot=(0,0,1;0rad)
  Support = -> [Pad025]
  TreeRank = 0
  ValidateShape = false
  sketch-geometry (2):
    g0: Circle CenterX=0 CenterY=0 CenterZ=0 NormalX=0 NormalY=0 NormalZ=1 AngleXU=0 Radius=3.125
    g1: Circle CenterX=0 CenterY=0 CenterZ=0 NormalX=0 NormalY=0 NormalZ=1 AngleXU=0 Radius=12.5
  constraints (4):
    c: Coincident(g0,g-1)
    c: Coincident(g1,g0)
    c: Diameter(g1) = 25
    c: Equal(g-3,g0)
FEATURE [PartDesign::Pad] Pad026
  AddSubType = 0
  AutoTaperInnerAngle = true
  BaseFeature = -> Pad025
  CheckUpToFaceLimits = true
  ClaimChildren = false
  Direction = (1,1,1)
  Fit = 0
  FitJoin = 0
  InnerFit = 0
  InnerFitJoin = 0
  InvalidShape = false
  Length = 2
  Length2 = 100
  NewSolid = false
  Profile = -> Sketch052
  Suppress = false
  TaperInnerAngle = 0
  TaperInnerAngleRev = 0
  TreeRank = 0
  Type = 0
  ValidateShape = true
  _ProfileBasedVersion = 0
FEATURE [PartDesign::Body] Body008
  AutoGroupSolids = false
  ClaimAllChildren = false
  ExportMode = 0
  Group = -> [Sketch051,Pad025,Sketch052,Pad026]
  InvalidShape = false
  Origin = -> Origin008
  SingleSolid = true
  Tip = -> Pad026
  TreeRank = 0
  ValidateShape = false
  _ExportChildren = -> [Pad025,Pad026]
  _GroupVersion = 1
COMPONENT P9 — recipe-attached ("Body009", modeled in this document).
Construction recipe (the document's own serialized feature program — sketch geometry with constraints, then the solid features built on it; lengths are millimeters unless a unit is written):

FEATURE [Sketcher::SketchObject] Sketch053
  ArcFitTolerance = 0
  ExternalBSplineMaxDegree = 0
  ExternalBSplineTolerance = 0
  FullyConstrained = false
  InternalTolerance = 1e-06
  InvalidShape = false
  MakeInternals = false
  MapMode = 5
  Placement = pos=(0,0,0) rot=(0,0.707107,0.707107;3.14159rad)
  TreeRank = 0
  ValidateShape = false
  sketch-geometry (10):
    g0: LineSegment [constr] StartX=0 StartY=0 StartZ=0 EndX=-55 EndY=0 EndZ=0
    g1: LineSegment [constr] StartX=-55 StartY=0 StartZ=0 EndX=-55 EndY=4.75 EndZ=0
    g2: LineSegment StartX=-52 StartY=0 StartZ=0 EndX=-58 EndY=0 EndZ=0
    g3: LineSegment StartX=-58 StartY=0 StartZ=0 EndX=-58 EndY=1.75 EndZ=0
    g4: LineSegment StartX=-52 StartY=0 StartZ=0 EndX=-52 EndY=1.75 EndZ=0
    g5: LineSegment StartX=-58 StartY=1.75 StartZ=0 EndX=-56 EndY=1.75 EndZ=0
    g6: LineSegment StartX=-52 StartY=1.75 StartZ=0 EndX=-54 EndY=1.75 EndZ=0
    g7: LineSegment StartX=-56 StartY=1.75 StartZ=0 EndX=-56 EndY=4.75 EndZ=0
    g8: LineSegment StartX=-56 StartY=4.75 StartZ=0 EndX=-54 EndY=4.75 EndZ=0
    g9: LineSegment StartX=-54 StartY=4.75 StartZ=0 EndX=-54 EndY=1.75 EndZ=0
  constraints (26):
    c: Coincident(g0,g-1)
    c: PointOnObject(g0,g-1)
    c: DistanceX(g0,g0) = 55
    c: Coincident(g1,g0)
    c: Vertical(g1)
    c: PointOnObject(g2,g0)
    c: Symmetric(g2,g2,g1)
    c: DistanceX(g2,g2) = 6
    c: Coincident(g3,g2)
    c: Coincident(g4,g2)
    c: Symmetric(g3,g4,g1)
    c: Vertical(g4)
    c: DistanceY(g3,g3) = 1.75
    c: Coincident(g5,g3)
    c: Coincident(g6,g4)
    c: Symmetric(g6,g5,g1)
    c: Horizontal(g5)
    c: DistanceX(g5,g5) = 2
    c: Coincident(g7,g5)
    c: Vertical(g7)
    c: Coincident(g8,g7)
    c: Coincident(g9,g8)
    c: Coincident(g9,g6)
    c: Symmetric(g7,g8,g1)
    c: DistanceY(g7,g7) = 3
    c: PointOnObject(g1,g8)
FEATURE [PartDesign::Revolution] Revolution002
  AddSubType = 0
  AllowMultiFace = false
  Angle = 360
  Axis = (-1e-16,2e-16,1)
  Base = (0,0,0)
  ClaimChildren = false
  Fit = 0
  FitJoin = 0
  InnerFit = 0
  InnerFitJoin = 0
  InvalidShape = false
  NewSolid = false
  Placement = pos=(0,0,0) rot=(0,0.707107,0.707107;3.14159rad)
  Profile = -> Sketch053
  ReferenceAxis = -> Sketch053 [V_Axis]
  Suppress = false
  TreeRank = 0
  ValidateShape = true
  _ProfileBasedVersion = 0
FEATURE [PartDesign::Draft] Draft005
  AddSubType = 0
  Angle = 5
  Base = -> Revolution002 [Face4,Face6]
  BaseFeature = -> Revolution002
  InvalidShape = false
  NeutralPlane = -> Revolution002 [Face3]
  NewSolid = false
  Placement = pos=(0,0,0) rot=(0,0.707107,0.707107;3.14159rad)
  Reversed = true
  SupportTransform = false
  Suppress = false
  TreeRank = 0
  ValidateShape = true
FEATURE [PartDesign::Body] Body009
  AutoGroupSolids = false
  ClaimAllChildren = false
  ExportMode = 0
  Group = -> [Sketch053,Revolution002,Draft005]
  InvalidShape = false
  Origin = -> Origin009
  SingleSolid = true
  Tip = -> Draft005
  TreeRank = 0
  ValidateShape = false
  _ExportChildren = -> [Revolution002,Draft005]
  _GroupVersion = 1
COMPONENT P10 — recipe-attached ("Body010", modeled in this document).
Construction recipe (the document's own serialized feature program — sketch geometry with constraints, then the solid features built on it; lengths are millimeters unless a unit is written):

FEATURE [Sketcher::SketchObject] Sketch054
  ArcFitTolerance = 0
  ExternalBSplineMaxDegree = 0
  ExternalBSplineTolerance = 0
  FullyConstrained = false
  InternalTolerance = 1e-06
  InvalidShape = false
  MakeInternals = false
  MapMode = 5
  Placement = pos=(0,0,0) rot=(0,0.707107,0.707107;3.14159rad)
  TreeRank = 0
  ValidateShape = false
  sketch-geometry (10):
    g0: LineSegment [constr] StartX=0 StartY=0 StartZ=0 EndX=-55 EndY=0 EndZ=0
    g1: LineSegment [constr] StartX=-55 StartY=0 StartZ=0 EndX=-55 EndY=4.75 EndZ=0
    g2: LineSegment StartX=-52 StartY=0 StartZ=0 EndX=-58 EndY=0 EndZ=0
    g3: LineSegment StartX=-58 StartY=0 StartZ=0 EndX=-58 EndY=1.75 EndZ=0
    g4: LineSegment StartX=-52 StartY=0 StartZ=0 EndX=-52 EndY=1.75 EndZ=0
    g5: LineSegment StartX=-58 StartY=1.75 StartZ=0 EndX=-56 EndY=1.75 EndZ=0
    g6: LineSegment StartX=-52 StartY=1.75 StartZ=0 EndX=-54 EndY=1.75 EndZ=0
    g7: LineSegment StartX=-56 StartY=1.75 StartZ=0 EndX=-56 EndY=4.75 EndZ=0
    g8: LineSegment StartX=-56 StartY=4.75 StartZ=0 EndX=-54 EndY=4.75 EndZ=0
    g9: LineSegment StartX=-54 StartY=4.75 StartZ=0 EndX=-54 EndY=1.75 EndZ=0
  constraints (26):
    c: Coincident(g0,g-1)
    c: PointOnObject(g0,g-1)
    c: DistanceX(g0,g0) = 55
    c: Coincident(g1,g0)
    c: Vertical(g1)
    c: PointOnObject(g2,g0)
    c: Symmetric(g2,g2,g1)
    c: DistanceX(g2,g2) = 6
    c: Coincident(g3,g2)
    c: Coincident(g4,g2)
    c: Symmetric(g3,g4,g1)
    c: Vertical(g4)
    c: DistanceY(g3,g3) = 1.75
    c: Coincident(g5,g3)
    c: Coincident(g6,g4)
    c: Symmetric(g6,g5,g1)
    c: Horizontal(g5)
    c: DistanceX(g5,g5) = 2
    c: Coincident(g7,g5)
    c: Vertical(g7)
    c: Coincident(g8,g7)
    c: Coincident(g9,g8)
    c: Coincident(g9,g6)
    c: Symmetric(g7,g8,g1)
    c: DistanceY(g7,g7) = 3
    c: PointOnObject(g1,g8)
FEATURE [PartDesign::Revolution] Revolution003
  AddSubType = 0
  AllowMultiFace = false
  Angle = 360
  Axis = (-1e-16,2e-16,1)
  Base = (0,0,0)
  ClaimChildren = false
  Fit = 0
  FitJoin = 0
  InnerFit = 0
  InnerFitJoin = 0
  InvalidShape = false
  NewSolid = false
  Placement = pos=(0,0,0) rot=(0,0.707107,0.707107;3.14159rad)
  Profile = -> Sketch054
  ReferenceAxis = -> Sketch054 [V_Axis]
  Suppress = false
  TreeRank = 0
  ValidateShape = true
  _ProfileBasedVersion = 0
FEATURE [PartDesign::Draft] Draft006
  AddSubType = 0
  Angle = 5
  Base = -> Revolution003 [Face4,Face6]
  BaseFeature = -> Revolution003
  InvalidShape = false
  NeutralPlane = -> Revolution003 [Face3]
  NewSolid = false
  Placement = pos=(0,0,0) rot=(0,0.707107,0.707107;3.14159rad)
  Reversed = true
  SupportTransform = false
  Suppress = false
  TreeRank = 0
  ValidateShape = true
FEATURE [PartDesign::Body] Body010
  AutoGroupSolids = false
  ClaimAllChildren = false
  ExportMode = 0
  Group = -> [Sketch054,Revolution003,Draft006]
  InvalidShape = false
  Origin = -> Origin010
  SingleSolid = true
  Tip = -> Draft006
  TreeRank = 0
  ValidateShape = false
  _ExportChildren = -> [Revolution003,Draft006]
  _GroupVersion = 1
